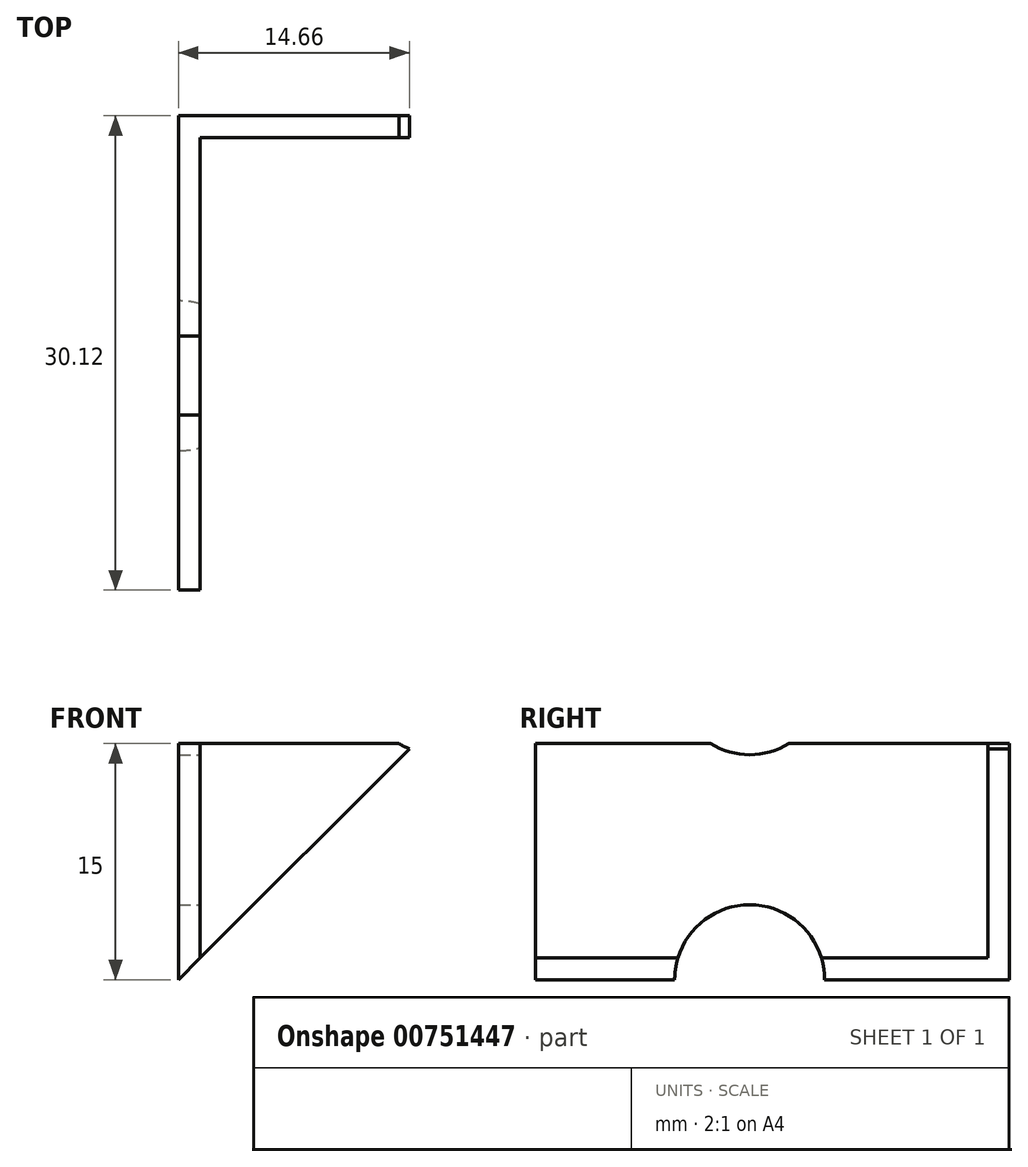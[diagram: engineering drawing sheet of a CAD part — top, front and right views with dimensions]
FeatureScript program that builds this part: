
annotation { "Feature Type Name" : "Feature", "Feature Type Description" : "" }
export const myFeature = defineFeature(function(context is Context, id is Id, definition is map)
    precondition{}
    {
        {
            assignVariable(context, id + "F0", {"name" : "height", "anyValue" : 15});
        }
        {
            var Q0;
            Q0=qCreatedBy(makeId("Top.planeOp"),FACE);
            var sketch = newSketch(context, id + "F1", { "sketchPlane" : qUnion([Q0])});
            skLineSegment(sketch, "E0", {"start": v(-1.37, -28.75) * mm, "end": v(-1.37, 1.37) * mm});
            skLineSegment(sketch, "E1", {"start": v(-1.37, 1.37) * mm, "end": v(28.75, 1.37) * mm});
            skLineSegment(sketch, "E2", {"start": v(28.75, 1.37) * mm, "end": v(28.75, 0) * mm});
            skLineSegment(sketch, "E3", {"start": v(28.75, 0) * mm, "end": v(0, 0) * mm});
            skLineSegment(sketch, "E4", {"start": v(0, 0) * mm, "end": v(0, -28.75) * mm});
            skLineSegment(sketch, "E5", {"start": v(0, -28.75) * mm, "end": v(-1.37, -28.75) * mm});
            skSolve(sketch);
        }
        {
            var Q0;
            Q0=makeQuery(id+"F1.imprint","IMPRINT",FACE,{"disambiguationData":[TD([[makeQuery(id+"F1.imprint","IMPRINT",EDGE,{"derivedFrom":sQuery(id+"F1.wireOp",EDGE,"E0")}),-1.0]])]});
            extrude(context, id + "F2", {"entities" : qUnion([Q0]), "depth" : (getVariable(context, 'height')) * mm, "offsetDistance" : 25.4 * mm});
        }
        {
            var Q0;
            Q0=makeQuery(id+"F2.opExtrude","SWEPT_FACE",FACE,{"disambiguationData":[OSD([sQuery(id+"F1.wireOp",EDGE,"E3")])]});
            var sketch = newSketch(context, id + "F3", { "sketchPlane" : qUnion([Q0])});
            skPoint(sketch, "E6", {"position": v(15.14, 19.05) * mm});
            skLineSegment(sketch, "E7", {"start": v(15.14, 0) * mm, "end": v(15.14, 381) * mm, "construction": true});
            skCircle(sketch, "E8", {"center": v(15.14, 19.05) * mm, "radius": 4.76 * mm});
            skCircle(sketch, "E9", {"center": v(15.14, 0) * mm, "radius": 4.76 * mm});
            skPoint(sketch, "E10", {"position": v(15.14, 38.1) * mm});
            skPoint(sketch, "E11", {"position": v(15.14, 57.15) * mm});
            skArc(sketch, "E12", {"start": v(19.9, 39.69) * mm, "mid": v(15.14, 44.45) * mm, "end": v(10.38, 39.69) * mm});
            skArc(sketch, "E13", {"start": v(10.38, 36.51) * mm, "mid": v(15.14, 31.75) * mm, "end": v(19.9, 36.51) * mm});
            skLineSegment(sketch, "E14", {"start": v(19.9, 39.69) * mm, "end": v(19.9, 36.51) * mm});
            skLineSegment(sketch, "E15", {"start": v(10.38, 39.69) * mm, "end": v(10.38, 36.51) * mm});
            skArc(sketch, "E16", {"start": v(19.9, 58.74) * mm, "mid": v(15.14, 63.5) * mm, "end": v(10.38, 58.74) * mm});
            skArc(sketch, "E17", {"start": v(10.38, 55.56) * mm, "mid": v(15.14, 50.8) * mm, "end": v(19.9, 55.56) * mm});
            skLineSegment(sketch, "E18", {"start": v(19.9, 58.74) * mm, "end": v(19.9, 55.56) * mm});
            skLineSegment(sketch, "E19", {"start": v(10.38, 58.74) * mm, "end": v(10.38, 55.56) * mm});
            skPoint(sketch, "E20.0.1.0", {"position": v(15.14, 133.35) * mm});
            skArc(sketch, "E20.0.1.1", {"start": v(19.9, 134.94) * mm, "mid": v(15.14, 139.7) * mm, "end": v(10.38, 134.94) * mm});
            skPoint(sketch, "E20.0.1.2", {"position": v(15.14, 114.3) * mm});
            skPoint(sketch, "E20.0.1.3", {"position": v(15.14, 95.25) * mm});
            skArc(sketch, "E20.0.1.4", {"start": v(10.38, 131.76) * mm, "mid": v(15.14, 127) * mm, "end": v(19.9, 131.76) * mm});
            skCircle(sketch, "E20.0.1.5", {"center": v(15.14, 95.25) * mm, "radius": 4.76 * mm});
            skCircle(sketch, "E20.0.1.6", {"center": v(15.14, 76.2) * mm, "radius": 4.76 * mm});
            skArc(sketch, "E20.0.1.7", {"start": v(19.9, 115.89) * mm, "mid": v(15.14, 120.65) * mm, "end": v(10.38, 115.89) * mm});
            skArc(sketch, "E20.0.1.8", {"start": v(10.38, 112.71) * mm, "mid": v(15.14, 107.95) * mm, "end": v(19.9, 112.71) * mm});
            skPoint(sketch, "E20.0.1.9", {"position": v(15.14, 133.35) * mm});
            skPoint(sketch, "E20.0.1.10", {"position": v(15.14, 114.3) * mm});
            skLineSegment(sketch, "E20.0.1.11", {"start": v(10.38, 134.94) * mm, "end": v(10.38, 131.76) * mm});
            skLineSegment(sketch, "E20.0.1.12", {"start": v(19.9, 134.94) * mm, "end": v(19.9, 131.76) * mm});
            skLineSegment(sketch, "E20.0.1.13", {"start": v(19.9, 115.89) * mm, "end": v(19.9, 112.71) * mm});
            skLineSegment(sketch, "E20.0.1.14", {"start": v(10.38, 115.89) * mm, "end": v(10.38, 112.71) * mm});
            skPoint(sketch, "E20.0.2.0", {"position": v(15.14, 209.55) * mm});
            skArc(sketch, "E20.0.2.1", {"start": v(19.9, 211.14) * mm, "mid": v(15.14, 215.9) * mm, "end": v(10.38, 211.14) * mm});
            skPoint(sketch, "E20.0.2.2", {"position": v(15.14, 190.5) * mm});
            skPoint(sketch, "E20.0.2.3", {"position": v(15.14, 171.45) * mm});
            skArc(sketch, "E20.0.2.4", {"start": v(10.38, 207.96) * mm, "mid": v(15.14, 203.2) * mm, "end": v(19.9, 207.96) * mm});
            skCircle(sketch, "E20.0.2.5", {"center": v(15.14, 171.45) * mm, "radius": 4.76 * mm});
            skCircle(sketch, "E20.0.2.6", {"center": v(15.14, 152.4) * mm, "radius": 4.76 * mm});
            skArc(sketch, "E20.0.2.7", {"start": v(19.9, 192.09) * mm, "mid": v(15.14, 196.85) * mm, "end": v(10.38, 192.09) * mm});
            skArc(sketch, "E20.0.2.8", {"start": v(10.38, 188.91) * mm, "mid": v(15.14, 184.15) * mm, "end": v(19.9, 188.91) * mm});
            skPoint(sketch, "E20.0.2.9", {"position": v(15.14, 209.55) * mm});
            skPoint(sketch, "E20.0.2.10", {"position": v(15.14, 190.5) * mm});
            skLineSegment(sketch, "E20.0.2.11", {"start": v(10.38, 211.14) * mm, "end": v(10.38, 207.96) * mm});
            skLineSegment(sketch, "E20.0.2.12", {"start": v(19.9, 211.14) * mm, "end": v(19.9, 207.96) * mm});
            skLineSegment(sketch, "E20.0.2.13", {"start": v(19.9, 192.09) * mm, "end": v(19.9, 188.91) * mm});
            skLineSegment(sketch, "E20.0.2.14", {"start": v(10.38, 192.09) * mm, "end": v(10.38, 188.91) * mm});
            skPoint(sketch, "E20.0.3.0", {"position": v(15.14, 285.75) * mm});
            skArc(sketch, "E20.0.3.1", {"start": v(19.9, 287.34) * mm, "mid": v(15.14, 292.1) * mm, "end": v(10.38, 287.34) * mm});
            skPoint(sketch, "E20.0.3.2", {"position": v(15.14, 266.7) * mm});
            skPoint(sketch, "E20.0.3.3", {"position": v(15.14, 247.65) * mm});
            skArc(sketch, "E20.0.3.4", {"start": v(10.38, 284.16) * mm, "mid": v(15.14, 279.4) * mm, "end": v(19.9, 284.16) * mm});
            skCircle(sketch, "E20.0.3.5", {"center": v(15.14, 247.65) * mm, "radius": 4.76 * mm});
            skCircle(sketch, "E20.0.3.6", {"center": v(15.14, 228.6) * mm, "radius": 4.76 * mm});
            skArc(sketch, "E20.0.3.7", {"start": v(19.9, 268.29) * mm, "mid": v(15.14, 273.05) * mm, "end": v(10.38, 268.29) * mm});
            skArc(sketch, "E20.0.3.8", {"start": v(10.38, 265.11) * mm, "mid": v(15.14, 260.35) * mm, "end": v(19.9, 265.11) * mm});
            skPoint(sketch, "E20.0.3.9", {"position": v(15.14, 285.75) * mm});
            skPoint(sketch, "E20.0.3.10", {"position": v(15.14, 266.7) * mm});
            skLineSegment(sketch, "E20.0.3.11", {"start": v(10.38, 287.34) * mm, "end": v(10.38, 284.16) * mm});
            skLineSegment(sketch, "E20.0.3.12", {"start": v(19.9, 287.34) * mm, "end": v(19.9, 284.16) * mm});
            skLineSegment(sketch, "E20.0.3.13", {"start": v(19.9, 268.29) * mm, "end": v(19.9, 265.11) * mm});
            skLineSegment(sketch, "E20.0.3.14", {"start": v(10.38, 268.29) * mm, "end": v(10.38, 265.11) * mm});
            skPoint(sketch, "E20.0.4.0", {"position": v(15.14, 361.95) * mm});
            skArc(sketch, "E20.0.4.1", {"start": v(19.9, 363.54) * mm, "mid": v(15.14, 368.3) * mm, "end": v(10.38, 363.54) * mm});
            skPoint(sketch, "E20.0.4.2", {"position": v(15.14, 342.9) * mm});
            skPoint(sketch, "E20.0.4.3", {"position": v(15.14, 323.85) * mm});
            skArc(sketch, "E20.0.4.4", {"start": v(10.38, 360.36) * mm, "mid": v(15.14, 355.6) * mm, "end": v(19.9, 360.36) * mm});
            skCircle(sketch, "E20.0.4.5", {"center": v(15.14, 323.85) * mm, "radius": 4.76 * mm});
            skCircle(sketch, "E20.0.4.6", {"center": v(15.14, 304.8) * mm, "radius": 4.76 * mm});
            skArc(sketch, "E20.0.4.7", {"start": v(19.9, 344.49) * mm, "mid": v(15.14, 349.25) * mm, "end": v(10.38, 344.49) * mm});
            skArc(sketch, "E20.0.4.8", {"start": v(10.38, 341.31) * mm, "mid": v(15.14, 336.55) * mm, "end": v(19.9, 341.31) * mm});
            skPoint(sketch, "E20.0.4.9", {"position": v(15.14, 361.95) * mm});
            skPoint(sketch, "E20.0.4.10", {"position": v(15.14, 342.9) * mm});
            skLineSegment(sketch, "E20.0.4.11", {"start": v(10.38, 363.54) * mm, "end": v(10.38, 360.36) * mm});
            skLineSegment(sketch, "E20.0.4.12", {"start": v(19.9, 363.54) * mm, "end": v(19.9, 360.36) * mm});
            skLineSegment(sketch, "E20.0.4.13", {"start": v(19.9, 344.49) * mm, "end": v(19.9, 341.31) * mm});
            skLineSegment(sketch, "E20.0.4.14", {"start": v(10.38, 344.49) * mm, "end": v(10.38, 341.31) * mm});
            skPoint(sketch, "E20.0.5.0", {"position": v(15.14, 438.15) * mm});
            skArc(sketch, "E20.0.5.1", {"start": v(19.9, 439.74) * mm, "mid": v(15.14, 444.5) * mm, "end": v(10.38, 439.74) * mm});
            skPoint(sketch, "E20.0.5.2", {"position": v(15.14, 419.1) * mm});
            skPoint(sketch, "E20.0.5.3", {"position": v(15.14, 400.05) * mm});
            skArc(sketch, "E20.0.5.4", {"start": v(10.38, 436.56) * mm, "mid": v(15.14, 431.8) * mm, "end": v(19.9, 436.56) * mm});
            skCircle(sketch, "E20.0.5.5", {"center": v(15.14, 400.05) * mm, "radius": 4.76 * mm});
            skCircle(sketch, "E20.0.5.6", {"center": v(15.14, 381) * mm, "radius": 4.76 * mm});
            skArc(sketch, "E20.0.5.7", {"start": v(19.9, 420.69) * mm, "mid": v(15.14, 425.45) * mm, "end": v(10.38, 420.69) * mm});
            skArc(sketch, "E20.0.5.8", {"start": v(10.38, 417.51) * mm, "mid": v(15.14, 412.75) * mm, "end": v(19.9, 417.51) * mm});
            skPoint(sketch, "E20.0.5.9", {"position": v(15.14, 438.15) * mm});
            skPoint(sketch, "E20.0.5.10", {"position": v(15.14, 419.1) * mm});
            skLineSegment(sketch, "E20.0.5.11", {"start": v(10.38, 439.74) * mm, "end": v(10.38, 436.56) * mm});
            skLineSegment(sketch, "E20.0.5.12", {"start": v(19.9, 439.74) * mm, "end": v(19.9, 436.56) * mm});
            skLineSegment(sketch, "E20.0.5.13", {"start": v(19.9, 420.69) * mm, "end": v(19.9, 417.51) * mm});
            skLineSegment(sketch, "E20.0.5.14", {"start": v(10.38, 420.69) * mm, "end": v(10.38, 417.51) * mm});
            skPoint(sketch, "E20.0.6.0", {"position": v(15.14, 514.35) * mm});
            skArc(sketch, "E20.0.6.1", {"start": v(19.9, 515.94) * mm, "mid": v(15.14, 520.7) * mm, "end": v(10.38, 515.94) * mm});
            skPoint(sketch, "E20.0.6.2", {"position": v(15.14, 495.3) * mm});
            skPoint(sketch, "E20.0.6.3", {"position": v(15.14, 476.25) * mm});
            skArc(sketch, "E20.0.6.4", {"start": v(10.38, 512.76) * mm, "mid": v(15.14, 508) * mm, "end": v(19.9, 512.76) * mm});
            skCircle(sketch, "E20.0.6.5", {"center": v(15.14, 476.25) * mm, "radius": 4.76 * mm});
            skCircle(sketch, "E20.0.6.6", {"center": v(15.14, 457.2) * mm, "radius": 4.76 * mm});
            skArc(sketch, "E20.0.6.7", {"start": v(19.9, 496.89) * mm, "mid": v(15.14, 501.65) * mm, "end": v(10.38, 496.89) * mm});
            skArc(sketch, "E20.0.6.8", {"start": v(10.38, 493.71) * mm, "mid": v(15.14, 488.95) * mm, "end": v(19.9, 493.71) * mm});
            skPoint(sketch, "E20.0.6.9", {"position": v(15.14, 514.35) * mm});
            skPoint(sketch, "E20.0.6.10", {"position": v(15.14, 495.3) * mm});
            skLineSegment(sketch, "E20.0.6.11", {"start": v(10.38, 515.94) * mm, "end": v(10.38, 512.76) * mm});
            skLineSegment(sketch, "E20.0.6.12", {"start": v(19.9, 515.94) * mm, "end": v(19.9, 512.76) * mm});
            skLineSegment(sketch, "E20.0.6.13", {"start": v(19.9, 496.89) * mm, "end": v(19.9, 493.71) * mm});
            skLineSegment(sketch, "E20.0.6.14", {"start": v(10.38, 496.89) * mm, "end": v(10.38, 493.71) * mm});
            skPoint(sketch, "E20.0.7.0", {"position": v(15.14, 590.55) * mm});
            skArc(sketch, "E20.0.7.1", {"start": v(19.9, 592.14) * mm, "mid": v(15.14, 596.9) * mm, "end": v(10.38, 592.14) * mm});
            skPoint(sketch, "E20.0.7.2", {"position": v(15.14, 571.5) * mm});
            skPoint(sketch, "E20.0.7.3", {"position": v(15.14, 552.45) * mm});
            skArc(sketch, "E20.0.7.4", {"start": v(10.38, 588.96) * mm, "mid": v(15.14, 584.2) * mm, "end": v(19.9, 588.96) * mm});
            skCircle(sketch, "E20.0.7.5", {"center": v(15.14, 552.45) * mm, "radius": 4.76 * mm});
            skCircle(sketch, "E20.0.7.6", {"center": v(15.14, 533.4) * mm, "radius": 4.76 * mm});
            skArc(sketch, "E20.0.7.7", {"start": v(19.9, 573.09) * mm, "mid": v(15.14, 577.85) * mm, "end": v(10.38, 573.09) * mm});
            skArc(sketch, "E20.0.7.8", {"start": v(10.38, 569.91) * mm, "mid": v(15.14, 565.15) * mm, "end": v(19.9, 569.91) * mm});
            skPoint(sketch, "E20.0.7.9", {"position": v(15.14, 590.55) * mm});
            skPoint(sketch, "E20.0.7.10", {"position": v(15.14, 571.5) * mm});
            skLineSegment(sketch, "E20.0.7.11", {"start": v(10.38, 592.14) * mm, "end": v(10.38, 588.96) * mm});
            skLineSegment(sketch, "E20.0.7.12", {"start": v(19.9, 592.14) * mm, "end": v(19.9, 588.96) * mm});
            skLineSegment(sketch, "E20.0.7.13", {"start": v(19.9, 573.09) * mm, "end": v(19.9, 569.91) * mm});
            skLineSegment(sketch, "E20.0.7.14", {"start": v(10.38, 573.09) * mm, "end": v(10.38, 569.91) * mm});
            skPoint(sketch, "E20.0.8.0", {"position": v(15.14, 666.75) * mm});
            skArc(sketch, "E20.0.8.1", {"start": v(19.9, 668.34) * mm, "mid": v(15.14, 673.1) * mm, "end": v(10.38, 668.34) * mm});
            skPoint(sketch, "E20.0.8.2", {"position": v(15.14, 647.7) * mm});
            skPoint(sketch, "E20.0.8.3", {"position": v(15.14, 628.65) * mm});
            skArc(sketch, "E20.0.8.4", {"start": v(10.38, 665.16) * mm, "mid": v(15.14, 660.4) * mm, "end": v(19.9, 665.16) * mm});
            skCircle(sketch, "E20.0.8.5", {"center": v(15.14, 628.65) * mm, "radius": 4.76 * mm});
            skCircle(sketch, "E20.0.8.6", {"center": v(15.14, 609.6) * mm, "radius": 4.76 * mm});
            skArc(sketch, "E20.0.8.7", {"start": v(19.9, 649.29) * mm, "mid": v(15.14, 654.05) * mm, "end": v(10.38, 649.29) * mm});
            skArc(sketch, "E20.0.8.8", {"start": v(10.38, 646.11) * mm, "mid": v(15.14, 641.35) * mm, "end": v(19.9, 646.11) * mm});
            skPoint(sketch, "E20.0.8.9", {"position": v(15.14, 666.75) * mm});
            skPoint(sketch, "E20.0.8.10", {"position": v(15.14, 647.7) * mm});
            skLineSegment(sketch, "E20.0.8.11", {"start": v(10.38, 668.34) * mm, "end": v(10.38, 665.16) * mm});
            skLineSegment(sketch, "E20.0.8.12", {"start": v(19.9, 668.34) * mm, "end": v(19.9, 665.16) * mm});
            skLineSegment(sketch, "E20.0.8.13", {"start": v(19.9, 649.29) * mm, "end": v(19.9, 646.11) * mm});
            skLineSegment(sketch, "E20.0.8.14", {"start": v(10.38, 649.29) * mm, "end": v(10.38, 646.11) * mm});
            skPoint(sketch, "E20.0.9.0", {"position": v(15.14, 742.95) * mm});
            skArc(sketch, "E20.0.9.1", {"start": v(19.9, 744.54) * mm, "mid": v(15.14, 749.3) * mm, "end": v(10.38, 744.54) * mm});
            skPoint(sketch, "E20.0.9.2", {"position": v(15.14, 723.9) * mm});
            skPoint(sketch, "E20.0.9.3", {"position": v(15.14, 704.85) * mm});
            skArc(sketch, "E20.0.9.4", {"start": v(10.38, 741.36) * mm, "mid": v(15.14, 736.6) * mm, "end": v(19.9, 741.36) * mm});
            skCircle(sketch, "E20.0.9.5", {"center": v(15.14, 704.85) * mm, "radius": 4.76 * mm});
            skCircle(sketch, "E20.0.9.6", {"center": v(15.14, 685.8) * mm, "radius": 4.76 * mm});
            skArc(sketch, "E20.0.9.7", {"start": v(19.9, 725.49) * mm, "mid": v(15.14, 730.25) * mm, "end": v(10.38, 725.49) * mm});
            skArc(sketch, "E20.0.9.8", {"start": v(10.38, 722.31) * mm, "mid": v(15.14, 717.55) * mm, "end": v(19.9, 722.31) * mm});
            skPoint(sketch, "E20.0.9.9", {"position": v(15.14, 742.95) * mm});
            skPoint(sketch, "E20.0.9.10", {"position": v(15.14, 723.9) * mm});
            skLineSegment(sketch, "E20.0.9.11", {"start": v(10.38, 744.54) * mm, "end": v(10.38, 741.36) * mm});
            skLineSegment(sketch, "E20.0.9.12", {"start": v(19.9, 744.54) * mm, "end": v(19.9, 741.36) * mm});
            skLineSegment(sketch, "E20.0.9.13", {"start": v(19.9, 725.49) * mm, "end": v(19.9, 722.31) * mm});
            skLineSegment(sketch, "E20.0.9.14", {"start": v(10.38, 725.49) * mm, "end": v(10.38, 722.31) * mm});
            skPoint(sketch, "E20.0.10.0", {"position": v(15.14, 819.15) * mm});
            skArc(sketch, "E20.0.10.1", {"start": v(19.9, 820.74) * mm, "mid": v(15.14, 825.5) * mm, "end": v(10.38, 820.74) * mm});
            skPoint(sketch, "E20.0.10.2", {"position": v(15.14, 800.1) * mm});
            skPoint(sketch, "E20.0.10.3", {"position": v(15.14, 781.05) * mm});
            skArc(sketch, "E20.0.10.4", {"start": v(10.38, 817.56) * mm, "mid": v(15.14, 812.8) * mm, "end": v(19.9, 817.56) * mm});
            skCircle(sketch, "E20.0.10.5", {"center": v(15.14, 781.05) * mm, "radius": 4.76 * mm});
            skCircle(sketch, "E20.0.10.6", {"center": v(15.14, 762) * mm, "radius": 4.76 * mm});
            skArc(sketch, "E20.0.10.7", {"start": v(19.9, 801.69) * mm, "mid": v(15.14, 806.45) * mm, "end": v(10.38, 801.69) * mm});
            skArc(sketch, "E20.0.10.8", {"start": v(10.38, 798.51) * mm, "mid": v(15.14, 793.75) * mm, "end": v(19.9, 798.51) * mm});
            skPoint(sketch, "E20.0.10.9", {"position": v(15.14, 819.15) * mm});
            skPoint(sketch, "E20.0.10.10", {"position": v(15.14, 800.1) * mm});
            skLineSegment(sketch, "E20.0.10.11", {"start": v(10.38, 820.74) * mm, "end": v(10.38, 817.56) * mm});
            skLineSegment(sketch, "E20.0.10.12", {"start": v(19.9, 820.74) * mm, "end": v(19.9, 817.56) * mm});
            skLineSegment(sketch, "E20.0.10.13", {"start": v(19.9, 801.69) * mm, "end": v(19.9, 798.51) * mm});
            skLineSegment(sketch, "E20.0.10.14", {"start": v(10.38, 801.69) * mm, "end": v(10.38, 798.51) * mm});
            skPoint(sketch, "E20.0.11.0", {"position": v(15.14, 895.35) * mm});
            skArc(sketch, "E20.0.11.1", {"start": v(19.9, 896.94) * mm, "mid": v(15.14, 901.7) * mm, "end": v(10.38, 896.94) * mm});
            skPoint(sketch, "E20.0.11.2", {"position": v(15.14, 876.3) * mm});
            skPoint(sketch, "E20.0.11.3", {"position": v(15.14, 857.25) * mm});
            skArc(sketch, "E20.0.11.4", {"start": v(10.38, 893.76) * mm, "mid": v(15.14, 889) * mm, "end": v(19.9, 893.76) * mm});
            skCircle(sketch, "E20.0.11.5", {"center": v(15.14, 857.25) * mm, "radius": 4.76 * mm});
            skCircle(sketch, "E20.0.11.6", {"center": v(15.14, 838.2) * mm, "radius": 4.76 * mm});
            skArc(sketch, "E20.0.11.7", {"start": v(19.9, 877.89) * mm, "mid": v(15.14, 882.65) * mm, "end": v(10.38, 877.89) * mm});
            skArc(sketch, "E20.0.11.8", {"start": v(10.38, 874.71) * mm, "mid": v(15.14, 869.95) * mm, "end": v(19.9, 874.71) * mm});
            skPoint(sketch, "E20.0.11.9", {"position": v(15.14, 895.35) * mm});
            skPoint(sketch, "E20.0.11.10", {"position": v(15.14, 876.3) * mm});
            skLineSegment(sketch, "E20.0.11.11", {"start": v(10.38, 896.94) * mm, "end": v(10.38, 893.76) * mm});
            skLineSegment(sketch, "E20.0.11.12", {"start": v(19.9, 896.94) * mm, "end": v(19.9, 893.76) * mm});
            skLineSegment(sketch, "E20.0.11.13", {"start": v(19.9, 877.89) * mm, "end": v(19.9, 874.71) * mm});
            skLineSegment(sketch, "E20.0.11.14", {"start": v(10.38, 877.89) * mm, "end": v(10.38, 874.71) * mm});
            skPoint(sketch, "E20.0.12.0", {"position": v(15.14, 971.55) * mm});
            skArc(sketch, "E20.0.12.1", {"start": v(19.9, 973.14) * mm, "mid": v(15.14, 977.9) * mm, "end": v(10.38, 973.14) * mm});
            skPoint(sketch, "E20.0.12.2", {"position": v(15.14, 952.5) * mm});
            skPoint(sketch, "E20.0.12.3", {"position": v(15.14, 933.45) * mm});
            skArc(sketch, "E20.0.12.4", {"start": v(10.38, 969.96) * mm, "mid": v(15.14, 965.2) * mm, "end": v(19.9, 969.96) * mm});
            skCircle(sketch, "E20.0.12.5", {"center": v(15.14, 933.45) * mm, "radius": 4.76 * mm});
            skCircle(sketch, "E20.0.12.6", {"center": v(15.14, 914.4) * mm, "radius": 4.76 * mm});
            skArc(sketch, "E20.0.12.7", {"start": v(19.9, 954.09) * mm, "mid": v(15.14, 958.85) * mm, "end": v(10.38, 954.09) * mm});
            skArc(sketch, "E20.0.12.8", {"start": v(10.38, 950.91) * mm, "mid": v(15.14, 946.15) * mm, "end": v(19.9, 950.91) * mm});
            skPoint(sketch, "E20.0.12.9", {"position": v(15.14, 971.55) * mm});
            skPoint(sketch, "E20.0.12.10", {"position": v(15.14, 952.5) * mm});
            skLineSegment(sketch, "E20.0.12.11", {"start": v(10.38, 973.14) * mm, "end": v(10.38, 969.96) * mm});
            skLineSegment(sketch, "E20.0.12.12", {"start": v(19.9, 973.14) * mm, "end": v(19.9, 969.96) * mm});
            skLineSegment(sketch, "E20.0.12.13", {"start": v(19.9, 954.09) * mm, "end": v(19.9, 950.91) * mm});
            skLineSegment(sketch, "E20.0.12.14", {"start": v(10.38, 954.09) * mm, "end": v(10.38, 950.91) * mm});
            skPoint(sketch, "E20.0.13.0", {"position": v(15.14, 1047.75) * mm});
            skArc(sketch, "E20.0.13.1", {"start": v(19.9, 1049.34) * mm, "mid": v(15.14, 1054.1) * mm, "end": v(10.38, 1049.34) * mm});
            skPoint(sketch, "E20.0.13.2", {"position": v(15.14, 1028.7) * mm});
            skPoint(sketch, "E20.0.13.3", {"position": v(15.14, 1009.65) * mm});
            skArc(sketch, "E20.0.13.4", {"start": v(10.38, 1046.16) * mm, "mid": v(15.14, 1041.4) * mm, "end": v(19.9, 1046.16) * mm});
            skCircle(sketch, "E20.0.13.5", {"center": v(15.14, 1009.65) * mm, "radius": 4.76 * mm});
            skCircle(sketch, "E20.0.13.6", {"center": v(15.14, 990.6) * mm, "radius": 4.76 * mm});
            skArc(sketch, "E20.0.13.7", {"start": v(19.9, 1030.29) * mm, "mid": v(15.14, 1035.05) * mm, "end": v(10.38, 1030.29) * mm});
            skArc(sketch, "E20.0.13.8", {"start": v(10.38, 1027.11) * mm, "mid": v(15.14, 1022.35) * mm, "end": v(19.9, 1027.11) * mm});
            skPoint(sketch, "E20.0.13.9", {"position": v(15.14, 1047.75) * mm});
            skPoint(sketch, "E20.0.13.10", {"position": v(15.14, 1028.7) * mm});
            skLineSegment(sketch, "E20.0.13.11", {"start": v(10.38, 1049.34) * mm, "end": v(10.38, 1046.16) * mm});
            skLineSegment(sketch, "E20.0.13.12", {"start": v(19.9, 1049.34) * mm, "end": v(19.9, 1046.16) * mm});
            skLineSegment(sketch, "E20.0.13.13", {"start": v(19.9, 1030.29) * mm, "end": v(19.9, 1027.11) * mm});
            skLineSegment(sketch, "E20.0.13.14", {"start": v(10.38, 1030.29) * mm, "end": v(10.38, 1027.11) * mm});
            skPoint(sketch, "E20.0.14.0", {"position": v(15.14, 1123.95) * mm});
            skArc(sketch, "E20.0.14.1", {"start": v(19.9, 1125.54) * mm, "mid": v(15.14, 1130.3) * mm, "end": v(10.38, 1125.54) * mm});
            skPoint(sketch, "E20.0.14.2", {"position": v(15.14, 1104.9) * mm});
            skPoint(sketch, "E20.0.14.3", {"position": v(15.14, 1085.85) * mm});
            skArc(sketch, "E20.0.14.4", {"start": v(10.38, 1122.36) * mm, "mid": v(15.14, 1117.6) * mm, "end": v(19.9, 1122.36) * mm});
            skCircle(sketch, "E20.0.14.5", {"center": v(15.14, 1085.85) * mm, "radius": 4.76 * mm});
            skCircle(sketch, "E20.0.14.6", {"center": v(15.14, 1066.8) * mm, "radius": 4.76 * mm});
            skArc(sketch, "E20.0.14.7", {"start": v(19.9, 1106.49) * mm, "mid": v(15.14, 1111.25) * mm, "end": v(10.38, 1106.49) * mm});
            skArc(sketch, "E20.0.14.8", {"start": v(10.38, 1103.31) * mm, "mid": v(15.14, 1098.55) * mm, "end": v(19.9, 1103.31) * mm});
            skPoint(sketch, "E20.0.14.9", {"position": v(15.14, 1123.95) * mm});
            skPoint(sketch, "E20.0.14.10", {"position": v(15.14, 1104.9) * mm});
            skLineSegment(sketch, "E20.0.14.11", {"start": v(10.38, 1125.54) * mm, "end": v(10.38, 1122.36) * mm});
            skLineSegment(sketch, "E20.0.14.12", {"start": v(19.9, 1125.54) * mm, "end": v(19.9, 1122.36) * mm});
            skLineSegment(sketch, "E20.0.14.13", {"start": v(19.9, 1106.49) * mm, "end": v(19.9, 1103.31) * mm});
            skLineSegment(sketch, "E20.0.14.14", {"start": v(10.38, 1106.49) * mm, "end": v(10.38, 1103.31) * mm});
            skPoint(sketch, "E20.0.15.0", {"position": v(15.14, 1200.15) * mm});
            skArc(sketch, "E20.0.15.1", {"start": v(19.9, 1201.74) * mm, "mid": v(15.14, 1206.5) * mm, "end": v(10.38, 1201.74) * mm});
            skPoint(sketch, "E20.0.15.2", {"position": v(15.14, 1181.1) * mm});
            skPoint(sketch, "E20.0.15.3", {"position": v(15.14, 1162.05) * mm});
            skArc(sketch, "E20.0.15.4", {"start": v(10.38, 1198.56) * mm, "mid": v(15.14, 1193.8) * mm, "end": v(19.9, 1198.56) * mm});
            skCircle(sketch, "E20.0.15.5", {"center": v(15.14, 1162.05) * mm, "radius": 4.76 * mm});
            skCircle(sketch, "E20.0.15.6", {"center": v(15.14, 1143) * mm, "radius": 4.76 * mm});
            skArc(sketch, "E20.0.15.7", {"start": v(19.9, 1182.69) * mm, "mid": v(15.14, 1187.45) * mm, "end": v(10.38, 1182.69) * mm});
            skArc(sketch, "E20.0.15.8", {"start": v(10.38, 1179.51) * mm, "mid": v(15.14, 1174.75) * mm, "end": v(19.9, 1179.51) * mm});
            skPoint(sketch, "E20.0.15.9", {"position": v(15.14, 1200.15) * mm});
            skPoint(sketch, "E20.0.15.10", {"position": v(15.14, 1181.1) * mm});
            skLineSegment(sketch, "E20.0.15.11", {"start": v(10.38, 1201.74) * mm, "end": v(10.38, 1198.56) * mm});
            skLineSegment(sketch, "E20.0.15.12", {"start": v(19.9, 1201.74) * mm, "end": v(19.9, 1198.56) * mm});
            skLineSegment(sketch, "E20.0.15.13", {"start": v(19.9, 1182.69) * mm, "end": v(19.9, 1179.51) * mm});
            skLineSegment(sketch, "E20.0.15.14", {"start": v(10.38, 1182.69) * mm, "end": v(10.38, 1179.51) * mm});
            skPoint(sketch, "E20.0.16.0", {"position": v(15.14, 1276.35) * mm});
            skArc(sketch, "E20.0.16.1", {"start": v(19.9, 1277.94) * mm, "mid": v(15.14, 1282.7) * mm, "end": v(10.38, 1277.94) * mm});
            skPoint(sketch, "E20.0.16.2", {"position": v(15.14, 1257.3) * mm});
            skPoint(sketch, "E20.0.16.3", {"position": v(15.14, 1238.25) * mm});
            skArc(sketch, "E20.0.16.4", {"start": v(10.38, 1274.76) * mm, "mid": v(15.14, 1270) * mm, "end": v(19.9, 1274.76) * mm});
            skCircle(sketch, "E20.0.16.5", {"center": v(15.14, 1238.25) * mm, "radius": 4.76 * mm});
            skCircle(sketch, "E20.0.16.6", {"center": v(15.14, 1219.2) * mm, "radius": 4.76 * mm});
            skArc(sketch, "E20.0.16.7", {"start": v(19.9, 1258.89) * mm, "mid": v(15.14, 1263.65) * mm, "end": v(10.38, 1258.89) * mm});
            skArc(sketch, "E20.0.16.8", {"start": v(10.38, 1255.71) * mm, "mid": v(15.14, 1250.95) * mm, "end": v(19.9, 1255.71) * mm});
            skPoint(sketch, "E20.0.16.9", {"position": v(15.14, 1276.35) * mm});
            skPoint(sketch, "E20.0.16.10", {"position": v(15.14, 1257.3) * mm});
            skLineSegment(sketch, "E20.0.16.11", {"start": v(10.38, 1277.94) * mm, "end": v(10.38, 1274.76) * mm});
            skLineSegment(sketch, "E20.0.16.12", {"start": v(19.9, 1277.94) * mm, "end": v(19.9, 1274.76) * mm});
            skLineSegment(sketch, "E20.0.16.13", {"start": v(19.9, 1258.89) * mm, "end": v(19.9, 1255.71) * mm});
            skLineSegment(sketch, "E20.0.16.14", {"start": v(10.38, 1258.89) * mm, "end": v(10.38, 1255.71) * mm});
            skPoint(sketch, "E20.0.17.0", {"position": v(15.14, 1352.55) * mm});
            skArc(sketch, "E20.0.17.1", {"start": v(19.9, 1354.14) * mm, "mid": v(15.14, 1358.9) * mm, "end": v(10.38, 1354.14) * mm});
            skPoint(sketch, "E20.0.17.2", {"position": v(15.14, 1333.5) * mm});
            skPoint(sketch, "E20.0.17.3", {"position": v(15.14, 1314.45) * mm});
            skArc(sketch, "E20.0.17.4", {"start": v(10.38, 1350.96) * mm, "mid": v(15.14, 1346.2) * mm, "end": v(19.9, 1350.96) * mm});
            skCircle(sketch, "E20.0.17.5", {"center": v(15.14, 1314.45) * mm, "radius": 4.76 * mm});
            skCircle(sketch, "E20.0.17.6", {"center": v(15.14, 1295.4) * mm, "radius": 4.76 * mm});
            skArc(sketch, "E20.0.17.7", {"start": v(19.9, 1335.09) * mm, "mid": v(15.14, 1339.85) * mm, "end": v(10.38, 1335.09) * mm});
            skArc(sketch, "E20.0.17.8", {"start": v(10.38, 1331.91) * mm, "mid": v(15.14, 1327.15) * mm, "end": v(19.9, 1331.91) * mm});
            skPoint(sketch, "E20.0.17.9", {"position": v(15.14, 1352.55) * mm});
            skPoint(sketch, "E20.0.17.10", {"position": v(15.14, 1333.5) * mm});
            skLineSegment(sketch, "E20.0.17.11", {"start": v(10.38, 1354.14) * mm, "end": v(10.38, 1350.96) * mm});
            skLineSegment(sketch, "E20.0.17.12", {"start": v(19.9, 1354.14) * mm, "end": v(19.9, 1350.96) * mm});
            skLineSegment(sketch, "E20.0.17.13", {"start": v(19.9, 1335.09) * mm, "end": v(19.9, 1331.91) * mm});
            skLineSegment(sketch, "E20.0.17.14", {"start": v(10.38, 1335.09) * mm, "end": v(10.38, 1331.91) * mm});
            skPoint(sketch, "E20.0.18.0", {"position": v(15.14, 1428.75) * mm});
            skArc(sketch, "E20.0.18.1", {"start": v(19.9, 1430.34) * mm, "mid": v(15.14, 1435.1) * mm, "end": v(10.38, 1430.34) * mm});
            skPoint(sketch, "E20.0.18.2", {"position": v(15.14, 1409.7) * mm});
            skPoint(sketch, "E20.0.18.3", {"position": v(15.14, 1390.65) * mm});
            skArc(sketch, "E20.0.18.4", {"start": v(10.38, 1427.16) * mm, "mid": v(15.14, 1422.4) * mm, "end": v(19.9, 1427.16) * mm});
            skCircle(sketch, "E20.0.18.5", {"center": v(15.14, 1390.65) * mm, "radius": 4.76 * mm});
            skCircle(sketch, "E20.0.18.6", {"center": v(15.14, 1371.6) * mm, "radius": 4.76 * mm});
            skArc(sketch, "E20.0.18.7", {"start": v(19.9, 1411.29) * mm, "mid": v(15.14, 1416.05) * mm, "end": v(10.38, 1411.29) * mm});
            skArc(sketch, "E20.0.18.8", {"start": v(10.38, 1408.11) * mm, "mid": v(15.14, 1403.35) * mm, "end": v(19.9, 1408.11) * mm});
            skPoint(sketch, "E20.0.18.9", {"position": v(15.14, 1428.75) * mm});
            skPoint(sketch, "E20.0.18.10", {"position": v(15.14, 1409.7) * mm});
            skLineSegment(sketch, "E20.0.18.11", {"start": v(10.38, 1430.34) * mm, "end": v(10.38, 1427.16) * mm});
            skLineSegment(sketch, "E20.0.18.12", {"start": v(19.9, 1430.34) * mm, "end": v(19.9, 1427.16) * mm});
            skLineSegment(sketch, "E20.0.18.13", {"start": v(19.9, 1411.29) * mm, "end": v(19.9, 1408.11) * mm});
            skLineSegment(sketch, "E20.0.18.14", {"start": v(10.38, 1411.29) * mm, "end": v(10.38, 1408.11) * mm});
            skPoint(sketch, "E20.0.19.0", {"position": v(15.14, 1504.95) * mm});
            skArc(sketch, "E20.0.19.1", {"start": v(19.9, 1506.54) * mm, "mid": v(15.14, 1511.3) * mm, "end": v(10.38, 1506.54) * mm});
            skPoint(sketch, "E20.0.19.2", {"position": v(15.14, 1485.9) * mm});
            skPoint(sketch, "E20.0.19.3", {"position": v(15.14, 1466.85) * mm});
            skArc(sketch, "E20.0.19.4", {"start": v(10.38, 1503.36) * mm, "mid": v(15.14, 1498.6) * mm, "end": v(19.9, 1503.36) * mm});
            skCircle(sketch, "E20.0.19.5", {"center": v(15.14, 1466.85) * mm, "radius": 4.76 * mm});
            skCircle(sketch, "E20.0.19.6", {"center": v(15.14, 1447.8) * mm, "radius": 4.76 * mm});
            skArc(sketch, "E20.0.19.7", {"start": v(19.9, 1487.49) * mm, "mid": v(15.14, 1492.25) * mm, "end": v(10.38, 1487.49) * mm});
            skArc(sketch, "E20.0.19.8", {"start": v(10.38, 1484.31) * mm, "mid": v(15.14, 1479.55) * mm, "end": v(19.9, 1484.31) * mm});
            skPoint(sketch, "E20.0.19.9", {"position": v(15.14, 1504.95) * mm});
            skPoint(sketch, "E20.0.19.10", {"position": v(15.14, 1485.9) * mm});
            skLineSegment(sketch, "E20.0.19.11", {"start": v(10.38, 1506.54) * mm, "end": v(10.38, 1503.36) * mm});
            skLineSegment(sketch, "E20.0.19.12", {"start": v(19.9, 1506.54) * mm, "end": v(19.9, 1503.36) * mm});
            skLineSegment(sketch, "E20.0.19.13", {"start": v(19.9, 1487.49) * mm, "end": v(19.9, 1484.31) * mm});
            skLineSegment(sketch, "E20.0.19.14", {"start": v(10.38, 1487.49) * mm, "end": v(10.38, 1484.31) * mm});
            skPoint(sketch, "E20.0.20.0", {"position": v(15.14, 1581.15) * mm});
            skArc(sketch, "E20.0.20.1", {"start": v(19.9, 1582.74) * mm, "mid": v(15.14, 1587.5) * mm, "end": v(10.38, 1582.74) * mm});
            skPoint(sketch, "E20.0.20.2", {"position": v(15.14, 1562.1) * mm});
            skPoint(sketch, "E20.0.20.3", {"position": v(15.14, 1543.05) * mm});
            skArc(sketch, "E20.0.20.4", {"start": v(10.38, 1579.56) * mm, "mid": v(15.14, 1574.8) * mm, "end": v(19.9, 1579.56) * mm});
            skCircle(sketch, "E20.0.20.5", {"center": v(15.14, 1543.05) * mm, "radius": 4.76 * mm});
            skCircle(sketch, "E20.0.20.6", {"center": v(15.14, 1524) * mm, "radius": 4.76 * mm});
            skArc(sketch, "E20.0.20.7", {"start": v(19.9, 1563.69) * mm, "mid": v(15.14, 1568.45) * mm, "end": v(10.38, 1563.69) * mm});
            skArc(sketch, "E20.0.20.8", {"start": v(10.38, 1560.51) * mm, "mid": v(15.14, 1555.75) * mm, "end": v(19.9, 1560.51) * mm});
            skPoint(sketch, "E20.0.20.9", {"position": v(15.14, 1581.15) * mm});
            skPoint(sketch, "E20.0.20.10", {"position": v(15.14, 1562.1) * mm});
            skLineSegment(sketch, "E20.0.20.11", {"start": v(10.38, 1582.74) * mm, "end": v(10.38, 1579.56) * mm});
            skLineSegment(sketch, "E20.0.20.12", {"start": v(19.9, 1582.74) * mm, "end": v(19.9, 1579.56) * mm});
            skLineSegment(sketch, "E20.0.20.13", {"start": v(19.9, 1563.69) * mm, "end": v(19.9, 1560.51) * mm});
            skLineSegment(sketch, "E20.0.20.14", {"start": v(10.38, 1563.69) * mm, "end": v(10.38, 1560.51) * mm});
            skPoint(sketch, "E20.0.21.0", {"position": v(15.14, 1657.35) * mm});
            skArc(sketch, "E20.0.21.1", {"start": v(19.9, 1658.94) * mm, "mid": v(15.14, 1663.7) * mm, "end": v(10.38, 1658.94) * mm});
            skPoint(sketch, "E20.0.21.2", {"position": v(15.14, 1638.3) * mm});
            skPoint(sketch, "E20.0.21.3", {"position": v(15.14, 1619.25) * mm});
            skArc(sketch, "E20.0.21.4", {"start": v(10.38, 1655.76) * mm, "mid": v(15.14, 1651) * mm, "end": v(19.9, 1655.76) * mm});
            skCircle(sketch, "E20.0.21.5", {"center": v(15.14, 1619.25) * mm, "radius": 4.76 * mm});
            skCircle(sketch, "E20.0.21.6", {"center": v(15.14, 1600.2) * mm, "radius": 4.76 * mm});
            skArc(sketch, "E20.0.21.7", {"start": v(19.9, 1639.89) * mm, "mid": v(15.14, 1644.65) * mm, "end": v(10.38, 1639.89) * mm});
            skArc(sketch, "E20.0.21.8", {"start": v(10.38, 1636.71) * mm, "mid": v(15.14, 1631.95) * mm, "end": v(19.9, 1636.71) * mm});
            skPoint(sketch, "E20.0.21.9", {"position": v(15.14, 1657.35) * mm});
            skPoint(sketch, "E20.0.21.10", {"position": v(15.14, 1638.3) * mm});
            skLineSegment(sketch, "E20.0.21.11", {"start": v(10.38, 1658.94) * mm, "end": v(10.38, 1655.76) * mm});
            skLineSegment(sketch, "E20.0.21.12", {"start": v(19.9, 1658.94) * mm, "end": v(19.9, 1655.76) * mm});
            skLineSegment(sketch, "E20.0.21.13", {"start": v(19.9, 1639.89) * mm, "end": v(19.9, 1636.71) * mm});
            skLineSegment(sketch, "E20.0.21.14", {"start": v(10.38, 1639.89) * mm, "end": v(10.38, 1636.71) * mm});
            skPoint(sketch, "E20.0.22.0", {"position": v(15.14, 1733.55) * mm});
            skArc(sketch, "E20.0.22.1", {"start": v(19.9, 1735.14) * mm, "mid": v(15.14, 1739.9) * mm, "end": v(10.38, 1735.14) * mm});
            skPoint(sketch, "E20.0.22.2", {"position": v(15.14, 1714.5) * mm});
            skPoint(sketch, "E20.0.22.3", {"position": v(15.14, 1695.45) * mm});
            skArc(sketch, "E20.0.22.4", {"start": v(10.38, 1731.96) * mm, "mid": v(15.14, 1727.2) * mm, "end": v(19.9, 1731.96) * mm});
            skCircle(sketch, "E20.0.22.5", {"center": v(15.14, 1695.45) * mm, "radius": 4.76 * mm});
            skCircle(sketch, "E20.0.22.6", {"center": v(15.14, 1676.4) * mm, "radius": 4.76 * mm});
            skArc(sketch, "E20.0.22.7", {"start": v(19.9, 1716.09) * mm, "mid": v(15.14, 1720.85) * mm, "end": v(10.38, 1716.09) * mm});
            skArc(sketch, "E20.0.22.8", {"start": v(10.38, 1712.91) * mm, "mid": v(15.14, 1708.15) * mm, "end": v(19.9, 1712.91) * mm});
            skPoint(sketch, "E20.0.22.9", {"position": v(15.14, 1733.55) * mm});
            skPoint(sketch, "E20.0.22.10", {"position": v(15.14, 1714.5) * mm});
            skLineSegment(sketch, "E20.0.22.11", {"start": v(10.38, 1735.14) * mm, "end": v(10.38, 1731.96) * mm});
            skLineSegment(sketch, "E20.0.22.12", {"start": v(19.9, 1735.14) * mm, "end": v(19.9, 1731.96) * mm});
            skLineSegment(sketch, "E20.0.22.13", {"start": v(19.9, 1716.09) * mm, "end": v(19.9, 1712.91) * mm});
            skLineSegment(sketch, "E20.0.22.14", {"start": v(10.38, 1716.09) * mm, "end": v(10.38, 1712.91) * mm});
            skPoint(sketch, "E20.0.23.0", {"position": v(15.14, 1809.75) * mm});
            skArc(sketch, "E20.0.23.1", {"start": v(19.9, 1811.34) * mm, "mid": v(15.14, 1816.1) * mm, "end": v(10.38, 1811.34) * mm});
            skPoint(sketch, "E20.0.23.2", {"position": v(15.14, 1790.7) * mm});
            skPoint(sketch, "E20.0.23.3", {"position": v(15.14, 1771.65) * mm});
            skArc(sketch, "E20.0.23.4", {"start": v(10.38, 1808.16) * mm, "mid": v(15.14, 1803.4) * mm, "end": v(19.9, 1808.16) * mm});
            skCircle(sketch, "E20.0.23.5", {"center": v(15.14, 1771.65) * mm, "radius": 4.76 * mm});
            skCircle(sketch, "E20.0.23.6", {"center": v(15.14, 1752.6) * mm, "radius": 4.76 * mm});
            skArc(sketch, "E20.0.23.7", {"start": v(19.9, 1792.29) * mm, "mid": v(15.14, 1797.05) * mm, "end": v(10.38, 1792.29) * mm});
            skArc(sketch, "E20.0.23.8", {"start": v(10.38, 1789.11) * mm, "mid": v(15.14, 1784.35) * mm, "end": v(19.9, 1789.11) * mm});
            skPoint(sketch, "E20.0.23.9", {"position": v(15.14, 1809.75) * mm});
            skPoint(sketch, "E20.0.23.10", {"position": v(15.14, 1790.7) * mm});
            skLineSegment(sketch, "E20.0.23.11", {"start": v(10.38, 1811.34) * mm, "end": v(10.38, 1808.16) * mm});
            skLineSegment(sketch, "E20.0.23.12", {"start": v(19.9, 1811.34) * mm, "end": v(19.9, 1808.16) * mm});
            skLineSegment(sketch, "E20.0.23.13", {"start": v(19.9, 1792.29) * mm, "end": v(19.9, 1789.11) * mm});
            skLineSegment(sketch, "E20.0.23.14", {"start": v(10.38, 1792.29) * mm, "end": v(10.38, 1789.11) * mm});
            skLineSegment(sketch, "E20.direction1", {"start": v(15.14, 0) * mm, "end": v(40.54, 0) * mm, "construction": true});
            skLineSegment(sketch, "E20.direction2", {"start": v(15.14, 0) * mm, "end": v(15.14, 76.2) * mm, "construction": true});
            skSolve(sketch);
        }
        {
            var Q0;
            Q0=makeQuery(id+"F2.opExtrude","SWEPT_FACE",FACE,{"disambiguationData":[OSD([sQuery(id+"F1.wireOp",EDGE,"E4")])]});
            var sketch = newSketch(context, id + "F4", { "sketchPlane" : qUnion([Q0])});
            skPoint(sketch, "E21", {"position": v(-15.14, 19.05) * mm});
            skLineSegment(sketch, "E22", {"start": v(-15.14, 0) * mm, "end": v(-15.14, 381) * mm, "construction": true});
            skCircle(sketch, "E23", {"center": v(-15.14, 19.05) * mm, "radius": 4.76 * mm});
            skCircle(sketch, "E24", {"center": v(-15.14, 0) * mm, "radius": 4.76 * mm});
            skPoint(sketch, "E25", {"position": v(-15.14, 38.1) * mm});
            skPoint(sketch, "E26", {"position": v(-15.14, 57.15) * mm});
            skArc(sketch, "E27", {"start": v(-10.38, 39.69) * mm, "mid": v(-15.14, 44.45) * mm, "end": v(-19.9, 39.69) * mm});
            skArc(sketch, "E28", {"start": v(-19.9, 36.51) * mm, "mid": v(-15.14, 31.75) * mm, "end": v(-10.38, 36.51) * mm});
            skLineSegment(sketch, "E29", {"start": v(-10.38, 39.69) * mm, "end": v(-10.38, 36.51) * mm});
            skLineSegment(sketch, "E30", {"start": v(-19.9, 39.69) * mm, "end": v(-19.9, 36.51) * mm});
            skArc(sketch, "E31", {"start": v(-10.38, 58.74) * mm, "mid": v(-15.14, 63.5) * mm, "end": v(-19.9, 58.74) * mm});
            skArc(sketch, "E32", {"start": v(-19.9, 55.56) * mm, "mid": v(-15.14, 50.8) * mm, "end": v(-10.38, 55.56) * mm});
            skLineSegment(sketch, "E33", {"start": v(-10.38, 58.74) * mm, "end": v(-10.38, 55.56) * mm});
            skLineSegment(sketch, "E34", {"start": v(-19.9, 58.74) * mm, "end": v(-19.9, 55.56) * mm});
            skPoint(sketch, "E35.0.1.0", {"position": v(-15.14, 133.35) * mm});
            skArc(sketch, "E35.0.1.1", {"start": v(-10.38, 134.94) * mm, "mid": v(-15.14, 139.7) * mm, "end": v(-19.9, 134.94) * mm});
            skPoint(sketch, "E35.0.1.2", {"position": v(-15.14, 114.3) * mm});
            skPoint(sketch, "E35.0.1.3", {"position": v(-15.14, 95.25) * mm});
            skArc(sketch, "E35.0.1.4", {"start": v(-19.9, 131.76) * mm, "mid": v(-15.14, 127) * mm, "end": v(-10.38, 131.76) * mm});
            skCircle(sketch, "E35.0.1.5", {"center": v(-15.14, 95.25) * mm, "radius": 4.76 * mm});
            skCircle(sketch, "E35.0.1.6", {"center": v(-15.14, 76.2) * mm, "radius": 4.76 * mm});
            skArc(sketch, "E35.0.1.7", {"start": v(-10.38, 115.89) * mm, "mid": v(-15.14, 120.65) * mm, "end": v(-19.9, 115.89) * mm});
            skArc(sketch, "E35.0.1.8", {"start": v(-19.9, 112.71) * mm, "mid": v(-15.14, 107.95) * mm, "end": v(-10.38, 112.71) * mm});
            skPoint(sketch, "E35.0.1.9", {"position": v(-15.14, 133.35) * mm});
            skPoint(sketch, "E35.0.1.10", {"position": v(-15.14, 114.3) * mm});
            skLineSegment(sketch, "E35.0.1.11", {"start": v(-19.9, 134.94) * mm, "end": v(-19.9, 131.76) * mm});
            skLineSegment(sketch, "E35.0.1.12", {"start": v(-10.38, 134.94) * mm, "end": v(-10.38, 131.76) * mm});
            skLineSegment(sketch, "E35.0.1.13", {"start": v(-10.38, 115.89) * mm, "end": v(-10.38, 112.71) * mm});
            skLineSegment(sketch, "E35.0.1.14", {"start": v(-19.9, 115.89) * mm, "end": v(-19.9, 112.71) * mm});
            skPoint(sketch, "E35.0.2.0", {"position": v(-15.14, 209.55) * mm});
            skArc(sketch, "E35.0.2.1", {"start": v(-10.38, 211.14) * mm, "mid": v(-15.14, 215.9) * mm, "end": v(-19.9, 211.14) * mm});
            skPoint(sketch, "E35.0.2.2", {"position": v(-15.14, 190.5) * mm});
            skPoint(sketch, "E35.0.2.3", {"position": v(-15.14, 171.45) * mm});
            skArc(sketch, "E35.0.2.4", {"start": v(-19.9, 207.96) * mm, "mid": v(-15.14, 203.2) * mm, "end": v(-10.38, 207.96) * mm});
            skCircle(sketch, "E35.0.2.5", {"center": v(-15.14, 171.45) * mm, "radius": 4.76 * mm});
            skCircle(sketch, "E35.0.2.6", {"center": v(-15.14, 152.4) * mm, "radius": 4.76 * mm});
            skArc(sketch, "E35.0.2.7", {"start": v(-10.38, 192.09) * mm, "mid": v(-15.14, 196.85) * mm, "end": v(-19.9, 192.09) * mm});
            skArc(sketch, "E35.0.2.8", {"start": v(-19.9, 188.91) * mm, "mid": v(-15.14, 184.15) * mm, "end": v(-10.38, 188.91) * mm});
            skPoint(sketch, "E35.0.2.9", {"position": v(-15.14, 209.55) * mm});
            skPoint(sketch, "E35.0.2.10", {"position": v(-15.14, 190.5) * mm});
            skLineSegment(sketch, "E35.0.2.11", {"start": v(-19.9, 211.14) * mm, "end": v(-19.9, 207.96) * mm});
            skLineSegment(sketch, "E35.0.2.12", {"start": v(-10.38, 211.14) * mm, "end": v(-10.38, 207.96) * mm});
            skLineSegment(sketch, "E35.0.2.13", {"start": v(-10.38, 192.09) * mm, "end": v(-10.38, 188.91) * mm});
            skLineSegment(sketch, "E35.0.2.14", {"start": v(-19.9, 192.09) * mm, "end": v(-19.9, 188.91) * mm});
            skPoint(sketch, "E35.0.3.0", {"position": v(-15.14, 285.75) * mm});
            skArc(sketch, "E35.0.3.1", {"start": v(-10.38, 287.34) * mm, "mid": v(-15.14, 292.1) * mm, "end": v(-19.9, 287.34) * mm});
            skPoint(sketch, "E35.0.3.2", {"position": v(-15.14, 266.7) * mm});
            skPoint(sketch, "E35.0.3.3", {"position": v(-15.14, 247.65) * mm});
            skArc(sketch, "E35.0.3.4", {"start": v(-19.9, 284.16) * mm, "mid": v(-15.14, 279.4) * mm, "end": v(-10.38, 284.16) * mm});
            skCircle(sketch, "E35.0.3.5", {"center": v(-15.14, 247.65) * mm, "radius": 4.76 * mm});
            skCircle(sketch, "E35.0.3.6", {"center": v(-15.14, 228.6) * mm, "radius": 4.76 * mm});
            skArc(sketch, "E35.0.3.7", {"start": v(-10.38, 268.29) * mm, "mid": v(-15.14, 273.05) * mm, "end": v(-19.9, 268.29) * mm});
            skArc(sketch, "E35.0.3.8", {"start": v(-19.9, 265.11) * mm, "mid": v(-15.14, 260.35) * mm, "end": v(-10.38, 265.11) * mm});
            skPoint(sketch, "E35.0.3.9", {"position": v(-15.14, 285.75) * mm});
            skPoint(sketch, "E35.0.3.10", {"position": v(-15.14, 266.7) * mm});
            skLineSegment(sketch, "E35.0.3.11", {"start": v(-19.9, 287.34) * mm, "end": v(-19.9, 284.16) * mm});
            skLineSegment(sketch, "E35.0.3.12", {"start": v(-10.38, 287.34) * mm, "end": v(-10.38, 284.16) * mm});
            skLineSegment(sketch, "E35.0.3.13", {"start": v(-10.38, 268.29) * mm, "end": v(-10.38, 265.11) * mm});
            skLineSegment(sketch, "E35.0.3.14", {"start": v(-19.9, 268.29) * mm, "end": v(-19.9, 265.11) * mm});
            skPoint(sketch, "E35.0.4.0", {"position": v(-15.14, 361.95) * mm});
            skArc(sketch, "E35.0.4.1", {"start": v(-10.38, 363.54) * mm, "mid": v(-15.14, 368.3) * mm, "end": v(-19.9, 363.54) * mm});
            skPoint(sketch, "E35.0.4.2", {"position": v(-15.14, 342.9) * mm});
            skPoint(sketch, "E35.0.4.3", {"position": v(-15.14, 323.85) * mm});
            skArc(sketch, "E35.0.4.4", {"start": v(-19.9, 360.36) * mm, "mid": v(-15.14, 355.6) * mm, "end": v(-10.38, 360.36) * mm});
            skCircle(sketch, "E35.0.4.5", {"center": v(-15.14, 323.85) * mm, "radius": 4.76 * mm});
            skCircle(sketch, "E35.0.4.6", {"center": v(-15.14, 304.8) * mm, "radius": 4.76 * mm});
            skArc(sketch, "E35.0.4.7", {"start": v(-10.38, 344.49) * mm, "mid": v(-15.14, 349.25) * mm, "end": v(-19.9, 344.49) * mm});
            skArc(sketch, "E35.0.4.8", {"start": v(-19.9, 341.31) * mm, "mid": v(-15.14, 336.55) * mm, "end": v(-10.38, 341.31) * mm});
            skPoint(sketch, "E35.0.4.9", {"position": v(-15.14, 361.95) * mm});
            skPoint(sketch, "E35.0.4.10", {"position": v(-15.14, 342.9) * mm});
            skLineSegment(sketch, "E35.0.4.11", {"start": v(-19.9, 363.54) * mm, "end": v(-19.9, 360.36) * mm});
            skLineSegment(sketch, "E35.0.4.12", {"start": v(-10.38, 363.54) * mm, "end": v(-10.38, 360.36) * mm});
            skLineSegment(sketch, "E35.0.4.13", {"start": v(-10.38, 344.49) * mm, "end": v(-10.38, 341.31) * mm});
            skLineSegment(sketch, "E35.0.4.14", {"start": v(-19.9, 344.49) * mm, "end": v(-19.9, 341.31) * mm});
            skPoint(sketch, "E35.0.5.0", {"position": v(-15.14, 438.15) * mm});
            skArc(sketch, "E35.0.5.1", {"start": v(-10.38, 439.74) * mm, "mid": v(-15.14, 444.5) * mm, "end": v(-19.9, 439.74) * mm});
            skPoint(sketch, "E35.0.5.2", {"position": v(-15.14, 419.1) * mm});
            skPoint(sketch, "E35.0.5.3", {"position": v(-15.14, 400.05) * mm});
            skArc(sketch, "E35.0.5.4", {"start": v(-19.9, 436.56) * mm, "mid": v(-15.14, 431.8) * mm, "end": v(-10.38, 436.56) * mm});
            skCircle(sketch, "E35.0.5.5", {"center": v(-15.14, 400.05) * mm, "radius": 4.76 * mm});
            skCircle(sketch, "E35.0.5.6", {"center": v(-15.14, 381) * mm, "radius": 4.76 * mm});
            skArc(sketch, "E35.0.5.7", {"start": v(-10.38, 420.69) * mm, "mid": v(-15.14, 425.45) * mm, "end": v(-19.9, 420.69) * mm});
            skArc(sketch, "E35.0.5.8", {"start": v(-19.9, 417.51) * mm, "mid": v(-15.14, 412.75) * mm, "end": v(-10.38, 417.51) * mm});
            skPoint(sketch, "E35.0.5.9", {"position": v(-15.14, 438.15) * mm});
            skPoint(sketch, "E35.0.5.10", {"position": v(-15.14, 419.1) * mm});
            skLineSegment(sketch, "E35.0.5.11", {"start": v(-19.9, 439.74) * mm, "end": v(-19.9, 436.56) * mm});
            skLineSegment(sketch, "E35.0.5.12", {"start": v(-10.38, 439.74) * mm, "end": v(-10.38, 436.56) * mm});
            skLineSegment(sketch, "E35.0.5.13", {"start": v(-10.38, 420.69) * mm, "end": v(-10.38, 417.51) * mm});
            skLineSegment(sketch, "E35.0.5.14", {"start": v(-19.9, 420.69) * mm, "end": v(-19.9, 417.51) * mm});
            skPoint(sketch, "E35.0.6.0", {"position": v(-15.14, 514.35) * mm});
            skArc(sketch, "E35.0.6.1", {"start": v(-10.38, 515.94) * mm, "mid": v(-15.14, 520.7) * mm, "end": v(-19.9, 515.94) * mm});
            skPoint(sketch, "E35.0.6.2", {"position": v(-15.14, 495.3) * mm});
            skPoint(sketch, "E35.0.6.3", {"position": v(-15.14, 476.25) * mm});
            skArc(sketch, "E35.0.6.4", {"start": v(-19.9, 512.76) * mm, "mid": v(-15.14, 508) * mm, "end": v(-10.38, 512.76) * mm});
            skCircle(sketch, "E35.0.6.5", {"center": v(-15.14, 476.25) * mm, "radius": 4.76 * mm});
            skCircle(sketch, "E35.0.6.6", {"center": v(-15.14, 457.2) * mm, "radius": 4.76 * mm});
            skArc(sketch, "E35.0.6.7", {"start": v(-10.38, 496.89) * mm, "mid": v(-15.14, 501.65) * mm, "end": v(-19.9, 496.89) * mm});
            skArc(sketch, "E35.0.6.8", {"start": v(-19.9, 493.71) * mm, "mid": v(-15.14, 488.95) * mm, "end": v(-10.38, 493.71) * mm});
            skPoint(sketch, "E35.0.6.9", {"position": v(-15.14, 514.35) * mm});
            skPoint(sketch, "E35.0.6.10", {"position": v(-15.14, 495.3) * mm});
            skLineSegment(sketch, "E35.0.6.11", {"start": v(-19.9, 515.94) * mm, "end": v(-19.9, 512.76) * mm});
            skLineSegment(sketch, "E35.0.6.12", {"start": v(-10.38, 515.94) * mm, "end": v(-10.38, 512.76) * mm});
            skLineSegment(sketch, "E35.0.6.13", {"start": v(-10.38, 496.89) * mm, "end": v(-10.38, 493.71) * mm});
            skLineSegment(sketch, "E35.0.6.14", {"start": v(-19.9, 496.89) * mm, "end": v(-19.9, 493.71) * mm});
            skPoint(sketch, "E35.0.7.0", {"position": v(-15.14, 590.55) * mm});
            skArc(sketch, "E35.0.7.1", {"start": v(-10.38, 592.14) * mm, "mid": v(-15.14, 596.9) * mm, "end": v(-19.9, 592.14) * mm});
            skPoint(sketch, "E35.0.7.2", {"position": v(-15.14, 571.5) * mm});
            skPoint(sketch, "E35.0.7.3", {"position": v(-15.14, 552.45) * mm});
            skArc(sketch, "E35.0.7.4", {"start": v(-19.9, 588.96) * mm, "mid": v(-15.14, 584.2) * mm, "end": v(-10.38, 588.96) * mm});
            skCircle(sketch, "E35.0.7.5", {"center": v(-15.14, 552.45) * mm, "radius": 4.76 * mm});
            skCircle(sketch, "E35.0.7.6", {"center": v(-15.14, 533.4) * mm, "radius": 4.76 * mm});
            skArc(sketch, "E35.0.7.7", {"start": v(-10.38, 573.09) * mm, "mid": v(-15.14, 577.85) * mm, "end": v(-19.9, 573.09) * mm});
            skArc(sketch, "E35.0.7.8", {"start": v(-19.9, 569.91) * mm, "mid": v(-15.14, 565.15) * mm, "end": v(-10.38, 569.91) * mm});
            skPoint(sketch, "E35.0.7.9", {"position": v(-15.14, 590.55) * mm});
            skPoint(sketch, "E35.0.7.10", {"position": v(-15.14, 571.5) * mm});
            skLineSegment(sketch, "E35.0.7.11", {"start": v(-19.9, 592.14) * mm, "end": v(-19.9, 588.96) * mm});
            skLineSegment(sketch, "E35.0.7.12", {"start": v(-10.38, 592.14) * mm, "end": v(-10.38, 588.96) * mm});
            skLineSegment(sketch, "E35.0.7.13", {"start": v(-10.38, 573.09) * mm, "end": v(-10.38, 569.91) * mm});
            skLineSegment(sketch, "E35.0.7.14", {"start": v(-19.9, 573.09) * mm, "end": v(-19.9, 569.91) * mm});
            skPoint(sketch, "E35.0.8.0", {"position": v(-15.14, 666.75) * mm});
            skArc(sketch, "E35.0.8.1", {"start": v(-10.38, 668.34) * mm, "mid": v(-15.14, 673.1) * mm, "end": v(-19.9, 668.34) * mm});
            skPoint(sketch, "E35.0.8.2", {"position": v(-15.14, 647.7) * mm});
            skPoint(sketch, "E35.0.8.3", {"position": v(-15.14, 628.65) * mm});
            skArc(sketch, "E35.0.8.4", {"start": v(-19.9, 665.16) * mm, "mid": v(-15.14, 660.4) * mm, "end": v(-10.38, 665.16) * mm});
            skCircle(sketch, "E35.0.8.5", {"center": v(-15.14, 628.65) * mm, "radius": 4.76 * mm});
            skCircle(sketch, "E35.0.8.6", {"center": v(-15.14, 609.6) * mm, "radius": 4.76 * mm});
            skArc(sketch, "E35.0.8.7", {"start": v(-10.38, 649.29) * mm, "mid": v(-15.14, 654.05) * mm, "end": v(-19.9, 649.29) * mm});
            skArc(sketch, "E35.0.8.8", {"start": v(-19.9, 646.11) * mm, "mid": v(-15.14, 641.35) * mm, "end": v(-10.38, 646.11) * mm});
            skPoint(sketch, "E35.0.8.9", {"position": v(-15.14, 666.75) * mm});
            skPoint(sketch, "E35.0.8.10", {"position": v(-15.14, 647.7) * mm});
            skLineSegment(sketch, "E35.0.8.11", {"start": v(-19.9, 668.34) * mm, "end": v(-19.9, 665.16) * mm});
            skLineSegment(sketch, "E35.0.8.12", {"start": v(-10.38, 668.34) * mm, "end": v(-10.38, 665.16) * mm});
            skLineSegment(sketch, "E35.0.8.13", {"start": v(-10.38, 649.29) * mm, "end": v(-10.38, 646.11) * mm});
            skLineSegment(sketch, "E35.0.8.14", {"start": v(-19.9, 649.29) * mm, "end": v(-19.9, 646.11) * mm});
            skPoint(sketch, "E35.0.9.0", {"position": v(-15.14, 742.95) * mm});
            skArc(sketch, "E35.0.9.1", {"start": v(-10.38, 744.54) * mm, "mid": v(-15.14, 749.3) * mm, "end": v(-19.9, 744.54) * mm});
            skPoint(sketch, "E35.0.9.2", {"position": v(-15.14, 723.9) * mm});
            skPoint(sketch, "E35.0.9.3", {"position": v(-15.14, 704.85) * mm});
            skArc(sketch, "E35.0.9.4", {"start": v(-19.9, 741.36) * mm, "mid": v(-15.14, 736.6) * mm, "end": v(-10.38, 741.36) * mm});
            skCircle(sketch, "E35.0.9.5", {"center": v(-15.14, 704.85) * mm, "radius": 4.76 * mm});
            skCircle(sketch, "E35.0.9.6", {"center": v(-15.14, 685.8) * mm, "radius": 4.76 * mm});
            skArc(sketch, "E35.0.9.7", {"start": v(-10.38, 725.49) * mm, "mid": v(-15.14, 730.25) * mm, "end": v(-19.9, 725.49) * mm});
            skArc(sketch, "E35.0.9.8", {"start": v(-19.9, 722.31) * mm, "mid": v(-15.14, 717.55) * mm, "end": v(-10.38, 722.31) * mm});
            skPoint(sketch, "E35.0.9.9", {"position": v(-15.14, 742.95) * mm});
            skPoint(sketch, "E35.0.9.10", {"position": v(-15.14, 723.9) * mm});
            skLineSegment(sketch, "E35.0.9.11", {"start": v(-19.9, 744.54) * mm, "end": v(-19.9, 741.36) * mm});
            skLineSegment(sketch, "E35.0.9.12", {"start": v(-10.38, 744.54) * mm, "end": v(-10.38, 741.36) * mm});
            skLineSegment(sketch, "E35.0.9.13", {"start": v(-10.38, 725.49) * mm, "end": v(-10.38, 722.31) * mm});
            skLineSegment(sketch, "E35.0.9.14", {"start": v(-19.9, 725.49) * mm, "end": v(-19.9, 722.31) * mm});
            skPoint(sketch, "E35.0.10.0", {"position": v(-15.14, 819.15) * mm});
            skArc(sketch, "E35.0.10.1", {"start": v(-10.38, 820.74) * mm, "mid": v(-15.14, 825.5) * mm, "end": v(-19.9, 820.74) * mm});
            skPoint(sketch, "E35.0.10.2", {"position": v(-15.14, 800.1) * mm});
            skPoint(sketch, "E35.0.10.3", {"position": v(-15.14, 781.05) * mm});
            skArc(sketch, "E35.0.10.4", {"start": v(-19.9, 817.56) * mm, "mid": v(-15.14, 812.8) * mm, "end": v(-10.38, 817.56) * mm});
            skCircle(sketch, "E35.0.10.5", {"center": v(-15.14, 781.05) * mm, "radius": 4.76 * mm});
            skCircle(sketch, "E35.0.10.6", {"center": v(-15.14, 762) * mm, "radius": 4.76 * mm});
            skArc(sketch, "E35.0.10.7", {"start": v(-10.38, 801.69) * mm, "mid": v(-15.14, 806.45) * mm, "end": v(-19.9, 801.69) * mm});
            skArc(sketch, "E35.0.10.8", {"start": v(-19.9, 798.51) * mm, "mid": v(-15.14, 793.75) * mm, "end": v(-10.38, 798.51) * mm});
            skPoint(sketch, "E35.0.10.9", {"position": v(-15.14, 819.15) * mm});
            skPoint(sketch, "E35.0.10.10", {"position": v(-15.14, 800.1) * mm});
            skLineSegment(sketch, "E35.0.10.11", {"start": v(-19.9, 820.74) * mm, "end": v(-19.9, 817.56) * mm});
            skLineSegment(sketch, "E35.0.10.12", {"start": v(-10.38, 820.74) * mm, "end": v(-10.38, 817.56) * mm});
            skLineSegment(sketch, "E35.0.10.13", {"start": v(-10.38, 801.69) * mm, "end": v(-10.38, 798.51) * mm});
            skLineSegment(sketch, "E35.0.10.14", {"start": v(-19.9, 801.69) * mm, "end": v(-19.9, 798.51) * mm});
            skPoint(sketch, "E35.0.11.0", {"position": v(-15.14, 895.35) * mm});
            skArc(sketch, "E35.0.11.1", {"start": v(-10.38, 896.94) * mm, "mid": v(-15.14, 901.7) * mm, "end": v(-19.9, 896.94) * mm});
            skPoint(sketch, "E35.0.11.2", {"position": v(-15.14, 876.3) * mm});
            skPoint(sketch, "E35.0.11.3", {"position": v(-15.14, 857.25) * mm});
            skArc(sketch, "E35.0.11.4", {"start": v(-19.9, 893.76) * mm, "mid": v(-15.14, 889) * mm, "end": v(-10.38, 893.76) * mm});
            skCircle(sketch, "E35.0.11.5", {"center": v(-15.14, 857.25) * mm, "radius": 4.76 * mm});
            skCircle(sketch, "E35.0.11.6", {"center": v(-15.14, 838.2) * mm, "radius": 4.76 * mm});
            skArc(sketch, "E35.0.11.7", {"start": v(-10.38, 877.89) * mm, "mid": v(-15.14, 882.65) * mm, "end": v(-19.9, 877.89) * mm});
            skArc(sketch, "E35.0.11.8", {"start": v(-19.9, 874.71) * mm, "mid": v(-15.14, 869.95) * mm, "end": v(-10.38, 874.71) * mm});
            skPoint(sketch, "E35.0.11.9", {"position": v(-15.14, 895.35) * mm});
            skPoint(sketch, "E35.0.11.10", {"position": v(-15.14, 876.3) * mm});
            skLineSegment(sketch, "E35.0.11.11", {"start": v(-19.9, 896.94) * mm, "end": v(-19.9, 893.76) * mm});
            skLineSegment(sketch, "E35.0.11.12", {"start": v(-10.38, 896.94) * mm, "end": v(-10.38, 893.76) * mm});
            skLineSegment(sketch, "E35.0.11.13", {"start": v(-10.38, 877.89) * mm, "end": v(-10.38, 874.71) * mm});
            skLineSegment(sketch, "E35.0.11.14", {"start": v(-19.9, 877.89) * mm, "end": v(-19.9, 874.71) * mm});
            skPoint(sketch, "E35.0.12.0", {"position": v(-15.14, 971.55) * mm});
            skArc(sketch, "E35.0.12.1", {"start": v(-10.38, 973.14) * mm, "mid": v(-15.14, 977.9) * mm, "end": v(-19.9, 973.14) * mm});
            skPoint(sketch, "E35.0.12.2", {"position": v(-15.14, 952.5) * mm});
            skPoint(sketch, "E35.0.12.3", {"position": v(-15.14, 933.45) * mm});
            skArc(sketch, "E35.0.12.4", {"start": v(-19.9, 969.96) * mm, "mid": v(-15.14, 965.2) * mm, "end": v(-10.38, 969.96) * mm});
            skCircle(sketch, "E35.0.12.5", {"center": v(-15.14, 933.45) * mm, "radius": 4.76 * mm});
            skCircle(sketch, "E35.0.12.6", {"center": v(-15.14, 914.4) * mm, "radius": 4.76 * mm});
            skArc(sketch, "E35.0.12.7", {"start": v(-10.38, 954.09) * mm, "mid": v(-15.14, 958.85) * mm, "end": v(-19.9, 954.09) * mm});
            skArc(sketch, "E35.0.12.8", {"start": v(-19.9, 950.91) * mm, "mid": v(-15.14, 946.15) * mm, "end": v(-10.38, 950.91) * mm});
            skPoint(sketch, "E35.0.12.9", {"position": v(-15.14, 971.55) * mm});
            skPoint(sketch, "E35.0.12.10", {"position": v(-15.14, 952.5) * mm});
            skLineSegment(sketch, "E35.0.12.11", {"start": v(-19.9, 973.14) * mm, "end": v(-19.9, 969.96) * mm});
            skLineSegment(sketch, "E35.0.12.12", {"start": v(-10.38, 973.14) * mm, "end": v(-10.38, 969.96) * mm});
            skLineSegment(sketch, "E35.0.12.13", {"start": v(-10.38, 954.09) * mm, "end": v(-10.38, 950.91) * mm});
            skLineSegment(sketch, "E35.0.12.14", {"start": v(-19.9, 954.09) * mm, "end": v(-19.9, 950.91) * mm});
            skPoint(sketch, "E35.0.13.0", {"position": v(-15.14, 1047.75) * mm});
            skArc(sketch, "E35.0.13.1", {"start": v(-10.38, 1049.34) * mm, "mid": v(-15.14, 1054.1) * mm, "end": v(-19.9, 1049.34) * mm});
            skPoint(sketch, "E35.0.13.2", {"position": v(-15.14, 1028.7) * mm});
            skPoint(sketch, "E35.0.13.3", {"position": v(-15.14, 1009.65) * mm});
            skArc(sketch, "E35.0.13.4", {"start": v(-19.9, 1046.16) * mm, "mid": v(-15.14, 1041.4) * mm, "end": v(-10.38, 1046.16) * mm});
            skCircle(sketch, "E35.0.13.5", {"center": v(-15.14, 1009.65) * mm, "radius": 4.76 * mm});
            skCircle(sketch, "E35.0.13.6", {"center": v(-15.14, 990.6) * mm, "radius": 4.76 * mm});
            skArc(sketch, "E35.0.13.7", {"start": v(-10.38, 1030.29) * mm, "mid": v(-15.14, 1035.05) * mm, "end": v(-19.9, 1030.29) * mm});
            skArc(sketch, "E35.0.13.8", {"start": v(-19.9, 1027.11) * mm, "mid": v(-15.14, 1022.35) * mm, "end": v(-10.38, 1027.11) * mm});
            skPoint(sketch, "E35.0.13.9", {"position": v(-15.14, 1047.75) * mm});
            skPoint(sketch, "E35.0.13.10", {"position": v(-15.14, 1028.7) * mm});
            skLineSegment(sketch, "E35.0.13.11", {"start": v(-19.9, 1049.34) * mm, "end": v(-19.9, 1046.16) * mm});
            skLineSegment(sketch, "E35.0.13.12", {"start": v(-10.38, 1049.34) * mm, "end": v(-10.38, 1046.16) * mm});
            skLineSegment(sketch, "E35.0.13.13", {"start": v(-10.38, 1030.29) * mm, "end": v(-10.38, 1027.11) * mm});
            skLineSegment(sketch, "E35.0.13.14", {"start": v(-19.9, 1030.29) * mm, "end": v(-19.9, 1027.11) * mm});
            skPoint(sketch, "E35.0.14.0", {"position": v(-15.14, 1123.95) * mm});
            skArc(sketch, "E35.0.14.1", {"start": v(-10.38, 1125.54) * mm, "mid": v(-15.14, 1130.3) * mm, "end": v(-19.9, 1125.54) * mm});
            skPoint(sketch, "E35.0.14.2", {"position": v(-15.14, 1104.9) * mm});
            skPoint(sketch, "E35.0.14.3", {"position": v(-15.14, 1085.85) * mm});
            skArc(sketch, "E35.0.14.4", {"start": v(-19.9, 1122.36) * mm, "mid": v(-15.14, 1117.6) * mm, "end": v(-10.38, 1122.36) * mm});
            skCircle(sketch, "E35.0.14.5", {"center": v(-15.14, 1085.85) * mm, "radius": 4.76 * mm});
            skCircle(sketch, "E35.0.14.6", {"center": v(-15.14, 1066.8) * mm, "radius": 4.76 * mm});
            skArc(sketch, "E35.0.14.7", {"start": v(-10.38, 1106.49) * mm, "mid": v(-15.14, 1111.25) * mm, "end": v(-19.9, 1106.49) * mm});
            skArc(sketch, "E35.0.14.8", {"start": v(-19.9, 1103.31) * mm, "mid": v(-15.14, 1098.55) * mm, "end": v(-10.38, 1103.31) * mm});
            skPoint(sketch, "E35.0.14.9", {"position": v(-15.14, 1123.95) * mm});
            skPoint(sketch, "E35.0.14.10", {"position": v(-15.14, 1104.9) * mm});
            skLineSegment(sketch, "E35.0.14.11", {"start": v(-19.9, 1125.54) * mm, "end": v(-19.9, 1122.36) * mm});
            skLineSegment(sketch, "E35.0.14.12", {"start": v(-10.38, 1125.54) * mm, "end": v(-10.38, 1122.36) * mm});
            skLineSegment(sketch, "E35.0.14.13", {"start": v(-10.38, 1106.49) * mm, "end": v(-10.38, 1103.31) * mm});
            skLineSegment(sketch, "E35.0.14.14", {"start": v(-19.9, 1106.49) * mm, "end": v(-19.9, 1103.31) * mm});
            skPoint(sketch, "E35.0.15.0", {"position": v(-15.14, 1200.15) * mm});
            skArc(sketch, "E35.0.15.1", {"start": v(-10.38, 1201.74) * mm, "mid": v(-15.14, 1206.5) * mm, "end": v(-19.9, 1201.74) * mm});
            skPoint(sketch, "E35.0.15.2", {"position": v(-15.14, 1181.1) * mm});
            skPoint(sketch, "E35.0.15.3", {"position": v(-15.14, 1162.05) * mm});
            skArc(sketch, "E35.0.15.4", {"start": v(-19.9, 1198.56) * mm, "mid": v(-15.14, 1193.8) * mm, "end": v(-10.38, 1198.56) * mm});
            skCircle(sketch, "E35.0.15.5", {"center": v(-15.14, 1162.05) * mm, "radius": 4.76 * mm});
            skCircle(sketch, "E35.0.15.6", {"center": v(-15.14, 1143) * mm, "radius": 4.76 * mm});
            skArc(sketch, "E35.0.15.7", {"start": v(-10.38, 1182.69) * mm, "mid": v(-15.14, 1187.45) * mm, "end": v(-19.9, 1182.69) * mm});
            skArc(sketch, "E35.0.15.8", {"start": v(-19.9, 1179.51) * mm, "mid": v(-15.14, 1174.75) * mm, "end": v(-10.38, 1179.51) * mm});
            skPoint(sketch, "E35.0.15.9", {"position": v(-15.14, 1200.15) * mm});
            skPoint(sketch, "E35.0.15.10", {"position": v(-15.14, 1181.1) * mm});
            skLineSegment(sketch, "E35.0.15.11", {"start": v(-19.9, 1201.74) * mm, "end": v(-19.9, 1198.56) * mm});
            skLineSegment(sketch, "E35.0.15.12", {"start": v(-10.38, 1201.74) * mm, "end": v(-10.38, 1198.56) * mm});
            skLineSegment(sketch, "E35.0.15.13", {"start": v(-10.38, 1182.69) * mm, "end": v(-10.38, 1179.51) * mm});
            skLineSegment(sketch, "E35.0.15.14", {"start": v(-19.9, 1182.69) * mm, "end": v(-19.9, 1179.51) * mm});
            skPoint(sketch, "E35.0.16.0", {"position": v(-15.14, 1276.35) * mm});
            skArc(sketch, "E35.0.16.1", {"start": v(-10.38, 1277.94) * mm, "mid": v(-15.14, 1282.7) * mm, "end": v(-19.9, 1277.94) * mm});
            skPoint(sketch, "E35.0.16.2", {"position": v(-15.14, 1257.3) * mm});
            skPoint(sketch, "E35.0.16.3", {"position": v(-15.14, 1238.25) * mm});
            skArc(sketch, "E35.0.16.4", {"start": v(-19.9, 1274.76) * mm, "mid": v(-15.14, 1270) * mm, "end": v(-10.38, 1274.76) * mm});
            skCircle(sketch, "E35.0.16.5", {"center": v(-15.14, 1238.25) * mm, "radius": 4.76 * mm});
            skCircle(sketch, "E35.0.16.6", {"center": v(-15.14, 1219.2) * mm, "radius": 4.76 * mm});
            skArc(sketch, "E35.0.16.7", {"start": v(-10.38, 1258.89) * mm, "mid": v(-15.14, 1263.65) * mm, "end": v(-19.9, 1258.89) * mm});
            skArc(sketch, "E35.0.16.8", {"start": v(-19.9, 1255.71) * mm, "mid": v(-15.14, 1250.95) * mm, "end": v(-10.38, 1255.71) * mm});
            skPoint(sketch, "E35.0.16.9", {"position": v(-15.14, 1276.35) * mm});
            skPoint(sketch, "E35.0.16.10", {"position": v(-15.14, 1257.3) * mm});
            skLineSegment(sketch, "E35.0.16.11", {"start": v(-19.9, 1277.94) * mm, "end": v(-19.9, 1274.76) * mm});
            skLineSegment(sketch, "E35.0.16.12", {"start": v(-10.38, 1277.94) * mm, "end": v(-10.38, 1274.76) * mm});
            skLineSegment(sketch, "E35.0.16.13", {"start": v(-10.38, 1258.89) * mm, "end": v(-10.38, 1255.71) * mm});
            skLineSegment(sketch, "E35.0.16.14", {"start": v(-19.9, 1258.89) * mm, "end": v(-19.9, 1255.71) * mm});
            skPoint(sketch, "E35.0.17.0", {"position": v(-15.14, 1352.55) * mm});
            skArc(sketch, "E35.0.17.1", {"start": v(-10.38, 1354.14) * mm, "mid": v(-15.14, 1358.9) * mm, "end": v(-19.9, 1354.14) * mm});
            skPoint(sketch, "E35.0.17.2", {"position": v(-15.14, 1333.5) * mm});
            skPoint(sketch, "E35.0.17.3", {"position": v(-15.14, 1314.45) * mm});
            skArc(sketch, "E35.0.17.4", {"start": v(-19.9, 1350.96) * mm, "mid": v(-15.14, 1346.2) * mm, "end": v(-10.38, 1350.96) * mm});
            skCircle(sketch, "E35.0.17.5", {"center": v(-15.14, 1314.45) * mm, "radius": 4.76 * mm});
            skCircle(sketch, "E35.0.17.6", {"center": v(-15.14, 1295.4) * mm, "radius": 4.76 * mm});
            skArc(sketch, "E35.0.17.7", {"start": v(-10.38, 1335.09) * mm, "mid": v(-15.14, 1339.85) * mm, "end": v(-19.9, 1335.09) * mm});
            skArc(sketch, "E35.0.17.8", {"start": v(-19.9, 1331.91) * mm, "mid": v(-15.14, 1327.15) * mm, "end": v(-10.38, 1331.91) * mm});
            skPoint(sketch, "E35.0.17.9", {"position": v(-15.14, 1352.55) * mm});
            skPoint(sketch, "E35.0.17.10", {"position": v(-15.14, 1333.5) * mm});
            skLineSegment(sketch, "E35.0.17.11", {"start": v(-19.9, 1354.14) * mm, "end": v(-19.9, 1350.96) * mm});
            skLineSegment(sketch, "E35.0.17.12", {"start": v(-10.38, 1354.14) * mm, "end": v(-10.38, 1350.96) * mm});
            skLineSegment(sketch, "E35.0.17.13", {"start": v(-10.38, 1335.09) * mm, "end": v(-10.38, 1331.91) * mm});
            skLineSegment(sketch, "E35.0.17.14", {"start": v(-19.9, 1335.09) * mm, "end": v(-19.9, 1331.91) * mm});
            skPoint(sketch, "E35.0.18.0", {"position": v(-15.14, 1428.75) * mm});
            skArc(sketch, "E35.0.18.1", {"start": v(-10.38, 1430.34) * mm, "mid": v(-15.14, 1435.1) * mm, "end": v(-19.9, 1430.34) * mm});
            skPoint(sketch, "E35.0.18.2", {"position": v(-15.14, 1409.7) * mm});
            skPoint(sketch, "E35.0.18.3", {"position": v(-15.14, 1390.65) * mm});
            skArc(sketch, "E35.0.18.4", {"start": v(-19.9, 1427.16) * mm, "mid": v(-15.14, 1422.4) * mm, "end": v(-10.38, 1427.16) * mm});
            skCircle(sketch, "E35.0.18.5", {"center": v(-15.14, 1390.65) * mm, "radius": 4.76 * mm});
            skCircle(sketch, "E35.0.18.6", {"center": v(-15.14, 1371.6) * mm, "radius": 4.76 * mm});
            skArc(sketch, "E35.0.18.7", {"start": v(-10.38, 1411.29) * mm, "mid": v(-15.14, 1416.05) * mm, "end": v(-19.9, 1411.29) * mm});
            skArc(sketch, "E35.0.18.8", {"start": v(-19.9, 1408.11) * mm, "mid": v(-15.14, 1403.35) * mm, "end": v(-10.38, 1408.11) * mm});
            skPoint(sketch, "E35.0.18.9", {"position": v(-15.14, 1428.75) * mm});
            skPoint(sketch, "E35.0.18.10", {"position": v(-15.14, 1409.7) * mm});
            skLineSegment(sketch, "E35.0.18.11", {"start": v(-19.9, 1430.34) * mm, "end": v(-19.9, 1427.16) * mm});
            skLineSegment(sketch, "E35.0.18.12", {"start": v(-10.38, 1430.34) * mm, "end": v(-10.38, 1427.16) * mm});
            skLineSegment(sketch, "E35.0.18.13", {"start": v(-10.38, 1411.29) * mm, "end": v(-10.38, 1408.11) * mm});
            skLineSegment(sketch, "E35.0.18.14", {"start": v(-19.9, 1411.29) * mm, "end": v(-19.9, 1408.11) * mm});
            skPoint(sketch, "E35.0.19.0", {"position": v(-15.14, 1504.95) * mm});
            skArc(sketch, "E35.0.19.1", {"start": v(-10.38, 1506.54) * mm, "mid": v(-15.14, 1511.3) * mm, "end": v(-19.9, 1506.54) * mm});
            skPoint(sketch, "E35.0.19.2", {"position": v(-15.14, 1485.9) * mm});
            skPoint(sketch, "E35.0.19.3", {"position": v(-15.14, 1466.85) * mm});
            skArc(sketch, "E35.0.19.4", {"start": v(-19.9, 1503.36) * mm, "mid": v(-15.14, 1498.6) * mm, "end": v(-10.38, 1503.36) * mm});
            skCircle(sketch, "E35.0.19.5", {"center": v(-15.14, 1466.85) * mm, "radius": 4.76 * mm});
            skCircle(sketch, "E35.0.19.6", {"center": v(-15.14, 1447.8) * mm, "radius": 4.76 * mm});
            skArc(sketch, "E35.0.19.7", {"start": v(-10.38, 1487.49) * mm, "mid": v(-15.14, 1492.25) * mm, "end": v(-19.9, 1487.49) * mm});
            skArc(sketch, "E35.0.19.8", {"start": v(-19.9, 1484.31) * mm, "mid": v(-15.14, 1479.55) * mm, "end": v(-10.38, 1484.31) * mm});
            skPoint(sketch, "E35.0.19.9", {"position": v(-15.14, 1504.95) * mm});
            skPoint(sketch, "E35.0.19.10", {"position": v(-15.14, 1485.9) * mm});
            skLineSegment(sketch, "E35.0.19.11", {"start": v(-19.9, 1506.54) * mm, "end": v(-19.9, 1503.36) * mm});
            skLineSegment(sketch, "E35.0.19.12", {"start": v(-10.38, 1506.54) * mm, "end": v(-10.38, 1503.36) * mm});
            skLineSegment(sketch, "E35.0.19.13", {"start": v(-10.38, 1487.49) * mm, "end": v(-10.38, 1484.31) * mm});
            skLineSegment(sketch, "E35.0.19.14", {"start": v(-19.9, 1487.49) * mm, "end": v(-19.9, 1484.31) * mm});
            skPoint(sketch, "E35.0.20.0", {"position": v(-15.14, 1581.15) * mm});
            skArc(sketch, "E35.0.20.1", {"start": v(-10.38, 1582.74) * mm, "mid": v(-15.14, 1587.5) * mm, "end": v(-19.9, 1582.74) * mm});
            skPoint(sketch, "E35.0.20.2", {"position": v(-15.14, 1562.1) * mm});
            skPoint(sketch, "E35.0.20.3", {"position": v(-15.14, 1543.05) * mm});
            skArc(sketch, "E35.0.20.4", {"start": v(-19.9, 1579.56) * mm, "mid": v(-15.14, 1574.8) * mm, "end": v(-10.38, 1579.56) * mm});
            skCircle(sketch, "E35.0.20.5", {"center": v(-15.14, 1543.05) * mm, "radius": 4.76 * mm});
            skCircle(sketch, "E35.0.20.6", {"center": v(-15.14, 1524) * mm, "radius": 4.76 * mm});
            skArc(sketch, "E35.0.20.7", {"start": v(-10.38, 1563.69) * mm, "mid": v(-15.14, 1568.45) * mm, "end": v(-19.9, 1563.69) * mm});
            skArc(sketch, "E35.0.20.8", {"start": v(-19.9, 1560.51) * mm, "mid": v(-15.14, 1555.75) * mm, "end": v(-10.38, 1560.51) * mm});
            skPoint(sketch, "E35.0.20.9", {"position": v(-15.14, 1581.15) * mm});
            skPoint(sketch, "E35.0.20.10", {"position": v(-15.14, 1562.1) * mm});
            skLineSegment(sketch, "E35.0.20.11", {"start": v(-19.9, 1582.74) * mm, "end": v(-19.9, 1579.56) * mm});
            skLineSegment(sketch, "E35.0.20.12", {"start": v(-10.38, 1582.74) * mm, "end": v(-10.38, 1579.56) * mm});
            skLineSegment(sketch, "E35.0.20.13", {"start": v(-10.38, 1563.69) * mm, "end": v(-10.38, 1560.51) * mm});
            skLineSegment(sketch, "E35.0.20.14", {"start": v(-19.9, 1563.69) * mm, "end": v(-19.9, 1560.51) * mm});
            skPoint(sketch, "E35.0.21.0", {"position": v(-15.14, 1657.35) * mm});
            skArc(sketch, "E35.0.21.1", {"start": v(-10.38, 1658.94) * mm, "mid": v(-15.14, 1663.7) * mm, "end": v(-19.9, 1658.94) * mm});
            skPoint(sketch, "E35.0.21.2", {"position": v(-15.14, 1638.3) * mm});
            skPoint(sketch, "E35.0.21.3", {"position": v(-15.14, 1619.25) * mm});
            skArc(sketch, "E35.0.21.4", {"start": v(-19.9, 1655.76) * mm, "mid": v(-15.14, 1651) * mm, "end": v(-10.38, 1655.76) * mm});
            skCircle(sketch, "E35.0.21.5", {"center": v(-15.14, 1619.25) * mm, "radius": 4.76 * mm});
            skCircle(sketch, "E35.0.21.6", {"center": v(-15.14, 1600.2) * mm, "radius": 4.76 * mm});
            skArc(sketch, "E35.0.21.7", {"start": v(-10.38, 1639.89) * mm, "mid": v(-15.14, 1644.65) * mm, "end": v(-19.9, 1639.89) * mm});
            skArc(sketch, "E35.0.21.8", {"start": v(-19.9, 1636.71) * mm, "mid": v(-15.14, 1631.95) * mm, "end": v(-10.38, 1636.71) * mm});
            skPoint(sketch, "E35.0.21.9", {"position": v(-15.14, 1657.35) * mm});
            skPoint(sketch, "E35.0.21.10", {"position": v(-15.14, 1638.3) * mm});
            skLineSegment(sketch, "E35.0.21.11", {"start": v(-19.9, 1658.94) * mm, "end": v(-19.9, 1655.76) * mm});
            skLineSegment(sketch, "E35.0.21.12", {"start": v(-10.38, 1658.94) * mm, "end": v(-10.38, 1655.76) * mm});
            skLineSegment(sketch, "E35.0.21.13", {"start": v(-10.38, 1639.89) * mm, "end": v(-10.38, 1636.71) * mm});
            skLineSegment(sketch, "E35.0.21.14", {"start": v(-19.9, 1639.89) * mm, "end": v(-19.9, 1636.71) * mm});
            skPoint(sketch, "E35.0.22.0", {"position": v(-15.14, 1733.55) * mm});
            skArc(sketch, "E35.0.22.1", {"start": v(-10.38, 1735.14) * mm, "mid": v(-15.14, 1739.9) * mm, "end": v(-19.9, 1735.14) * mm});
            skPoint(sketch, "E35.0.22.2", {"position": v(-15.14, 1714.5) * mm});
            skPoint(sketch, "E35.0.22.3", {"position": v(-15.14, 1695.45) * mm});
            skArc(sketch, "E35.0.22.4", {"start": v(-19.9, 1731.96) * mm, "mid": v(-15.14, 1727.2) * mm, "end": v(-10.38, 1731.96) * mm});
            skCircle(sketch, "E35.0.22.5", {"center": v(-15.14, 1695.45) * mm, "radius": 4.76 * mm});
            skCircle(sketch, "E35.0.22.6", {"center": v(-15.14, 1676.4) * mm, "radius": 4.76 * mm});
            skArc(sketch, "E35.0.22.7", {"start": v(-10.38, 1716.09) * mm, "mid": v(-15.14, 1720.85) * mm, "end": v(-19.9, 1716.09) * mm});
            skArc(sketch, "E35.0.22.8", {"start": v(-19.9, 1712.91) * mm, "mid": v(-15.14, 1708.15) * mm, "end": v(-10.38, 1712.91) * mm});
            skPoint(sketch, "E35.0.22.9", {"position": v(-15.14, 1733.55) * mm});
            skPoint(sketch, "E35.0.22.10", {"position": v(-15.14, 1714.5) * mm});
            skLineSegment(sketch, "E35.0.22.11", {"start": v(-19.9, 1735.14) * mm, "end": v(-19.9, 1731.96) * mm});
            skLineSegment(sketch, "E35.0.22.12", {"start": v(-10.38, 1735.14) * mm, "end": v(-10.38, 1731.96) * mm});
            skLineSegment(sketch, "E35.0.22.13", {"start": v(-10.38, 1716.09) * mm, "end": v(-10.38, 1712.91) * mm});
            skLineSegment(sketch, "E35.0.22.14", {"start": v(-19.9, 1716.09) * mm, "end": v(-19.9, 1712.91) * mm});
            skPoint(sketch, "E35.0.23.0", {"position": v(-15.14, 1809.75) * mm});
            skArc(sketch, "E35.0.23.1", {"start": v(-10.38, 1811.34) * mm, "mid": v(-15.14, 1816.1) * mm, "end": v(-19.9, 1811.34) * mm});
            skPoint(sketch, "E35.0.23.2", {"position": v(-15.14, 1790.7) * mm});
            skPoint(sketch, "E35.0.23.3", {"position": v(-15.14, 1771.65) * mm});
            skArc(sketch, "E35.0.23.4", {"start": v(-19.9, 1808.16) * mm, "mid": v(-15.14, 1803.4) * mm, "end": v(-10.38, 1808.16) * mm});
            skCircle(sketch, "E35.0.23.5", {"center": v(-15.14, 1771.65) * mm, "radius": 4.76 * mm});
            skCircle(sketch, "E35.0.23.6", {"center": v(-15.14, 1752.6) * mm, "radius": 4.76 * mm});
            skArc(sketch, "E35.0.23.7", {"start": v(-10.38, 1792.29) * mm, "mid": v(-15.14, 1797.05) * mm, "end": v(-19.9, 1792.29) * mm});
            skArc(sketch, "E35.0.23.8", {"start": v(-19.9, 1789.11) * mm, "mid": v(-15.14, 1784.35) * mm, "end": v(-10.38, 1789.11) * mm});
            skPoint(sketch, "E35.0.23.9", {"position": v(-15.14, 1809.75) * mm});
            skPoint(sketch, "E35.0.23.10", {"position": v(-15.14, 1790.7) * mm});
            skLineSegment(sketch, "E35.0.23.11", {"start": v(-19.9, 1811.34) * mm, "end": v(-19.9, 1808.16) * mm});
            skLineSegment(sketch, "E35.0.23.12", {"start": v(-10.38, 1811.34) * mm, "end": v(-10.38, 1808.16) * mm});
            skLineSegment(sketch, "E35.0.23.13", {"start": v(-10.38, 1792.29) * mm, "end": v(-10.38, 1789.11) * mm});
            skLineSegment(sketch, "E35.0.23.14", {"start": v(-19.9, 1792.29) * mm, "end": v(-19.9, 1789.11) * mm});
            skLineSegment(sketch, "E35.direction1", {"start": v(-15.14, 0) * mm, "end": v(10.99, 0) * mm, "construction": true});
            skLineSegment(sketch, "E35.direction2", {"start": v(-15.14, 0) * mm, "end": v(-15.14, 76.2) * mm, "construction": true});
            skSolve(sketch);
        }
        {
            var Q0;
            Q0=qSketchRegion(id+"F3",true);
            extrude(context, id + "F5", {"entities" : qUnion([Q0]), "operationType" : NewBodyOperationType.REMOVE, "endBound" : BoundingType.THROUGH_ALL, "oppositeDirection" : true, "depth" : 25.4 * mm, "offsetDistance" : 25.4 * mm});
        }
        {
            var Q0;
            Q0=qSketchRegion(id+"F4",true);
            extrude(context, id + "F6", {"entities" : qUnion([Q0]), "operationType" : NewBodyOperationType.REMOVE, "endBound" : BoundingType.THROUGH_ALL, "oppositeDirection" : true, "depth" : 25.4 * mm, "offsetDistance" : 25.4 * mm});
        }
        {
            var Q0;
            Q0=makeQuery(id+"F2.opExtrude","SWEPT_FACE",FACE,{"disambiguationData":[OSD([sQuery(id+"F1.wireOp",EDGE,"E1")])]});
            var sketch = newSketch(context, id + "F7", { "sketchPlane" : qUnion([Q0])});
            skLineSegment(sketch, "E36", {"start": v(1.37, 381) * mm, "end": v(-28.75, 381) * mm});
            skLineSegment(sketch, "E37", {"start": v(-28.75, 381) * mm, "end": v(-28.75, 350.88) * mm});
            skLineSegment(sketch, "E38", {"start": v(-28.75, 350.88) * mm, "end": v(1.37, 381) * mm});
            skLineSegment(sketch, "E39", {"start": v(-28.75, 0) * mm, "end": v(1.37, 0) * mm});
            skLineSegment(sketch, "E40", {"start": v(1.37, 0) * mm, "end": v(-28.75, 30.12) * mm});
            skLineSegment(sketch, "E41", {"start": v(-28.75, 30.12) * mm, "end": v(-28.75, 0) * mm});
            skSolve(sketch);
        }
        {
            var Q0;
            Q0=qSketchRegion(id+"F7",true);
            extrude(context, id + "F8", {"entities" : qUnion([Q0]), "operationType" : NewBodyOperationType.REMOVE, "endBound" : BoundingType.THROUGH_ALL, "oppositeDirection" : true, "depth" : 25.4 * mm, "offsetDistance" : 25.4 * mm});
        }
        {
            var Q0;
            Q0=makeQuery(id+"F2.opExtrude","SWEPT_FACE",FACE,{"disambiguationData":[OSD([sQuery(id+"F1.wireOp",EDGE,"E0")])]});
            var sketch = newSketch(context, id + "F9", { "sketchPlane" : qUnion([Q0])});
            skCircle(sketch, "E42", {"center": v(17.68, 276.22) * mm, "radius": 9.53 * mm});
            skLineSegment(sketch, "E43", {"start": v(15.14, 279.4) * mm, "end": v(15.14, 273.05) * mm, "construction": true});
            skPoint(sketch, "E44", {"position": v(15.14, 276.22) * mm});
            skLineSegment(sketch, "E45", {"start": v(15.14, 90.49) * mm, "end": v(15.14, 80.96) * mm, "construction": true});
            skPoint(sketch, "E45.startSnap0", {"position": v(15.14, 44.45) * mm});
            skPoint(sketch, "E46", {"position": v(15.14, 85.72) * mm});
            skCircle(sketch, "E47", {"center": v(17.68, 85.72) * mm, "radius": 9.53 * mm});
            skSolve(sketch);
        }
        {
            var Q0;
            {var subQ0=makeQuery(id+"F2.opExtrude","SWEPT_FACE",FACE,{"disambiguationData":[OSD([sQuery(id+"F1.wireOp",EDGE,"E0")])]});var subQ4=sQuery(id+"F9.wireOp",EDGE,"E42");var subQ7=makeQuery(id+"F6.boolean.opBoolean","INTERSECT",EDGE,{"derivedFrom":[subQ0,makeQuery(id+"F6.opExtrude","SWEPT_FACE",FACE,{"disambiguationData":[OSD([sQuery(id+"F4.wireOp",EDGE,"E35.0.3.4")])]})]});var subQ9=makeQuery(id+"F9.imprint","INTERSECT",VERTEX,{"derivedFrom":[subQ7,subQ4]});Q0=makeQuery(id+"F9.imprint","IMPRINT",FACE,{"disambiguationData":[TD([[makeQuery(id+"F9.imprint","IMPRINT",EDGE,{"disambiguationData":[TD([[subQ9,-1.0]])],"derivedFrom":subQ4}),1.0]])]});}
            var Q1;
            {var subQ0=sQuery(id+"F9.wireOp",EDGE,"E47");var subQ1=makeQuery(id+"F2.opExtrude","SWEPT_FACE",FACE,{"disambiguationData":[OSD([sQuery(id+"F1.wireOp",EDGE,"E0")])]});var subQ2=makeQuery(id+"F6.boolean.opBoolean","INTERSECT",EDGE,{"derivedFrom":[subQ1,makeQuery(id+"F6.opExtrude","SWEPT_FACE",FACE,{"disambiguationData":[OSD([sQuery(id+"F4.wireOp",EDGE,"E35.0.1.5")])]})]});var subQ3=makeQuery(id+"F9.imprint","INTERSECT",VERTEX,{"disambiguationData":[OD(0.0)],"derivedFrom":[subQ2,subQ0]});Q1=makeQuery(id+"F9.imprint","IMPRINT",FACE,{"disambiguationData":[TD([[makeQuery(id+"F9.imprint","IMPRINT",EDGE,{"disambiguationData":[TD([[subQ3,-1.0]])],"derivedFrom":subQ0}),1.0]])]});}
            extrude(context, id + "F10", {"entities" : qUnion([Q0, Q1]), "operationType" : NewBodyOperationType.REMOVE, "endBound" : BoundingType.THROUGH_ALL, "oppositeDirection" : true, "depth" : 25.4 * mm, "offsetDistance" : 25.4 * mm});
        }
        {
            var Q0;
            Q0=makeQuery(id+"F2.opExtrude","SWEPT_FACE",FACE,{"disambiguationData":[OSD([sQuery(id+"F1.wireOp",EDGE,"E0")])]});
            var sketch = newSketch(context, id + "F11", { "sketchPlane" : qUnion([Q0])});
            skLineSegment(sketch, "E48", {"start": v(19.9, 361.95) * mm, "end": v(10.38, 361.95) * mm, "construction": true});
            skPoint(sketch, "E49", {"position": v(15.14, 361.95) * mm});
            skSolve(sketch);
        }
        {
            var Q0;
            Q0=makeQuery(id+"F2.opExtrude","SWEPT_FACE",FACE,{"disambiguationData":[OSD([sQuery(id+"F1.wireOp",EDGE,"E4")])]});
            var sketch = newSketch(context, id + "F12", { "sketchPlane" : qUnion([Q0])});
            skLineSegment(sketch, "E50", {"start": v(-10.38, 361.95) * mm, "end": v(-19.9, 361.95) * mm, "construction": true});
            skPoint(sketch, "E51", {"position": v(-15.14, 361.95) * mm});
            skSolve(sketch);
        }
    });
